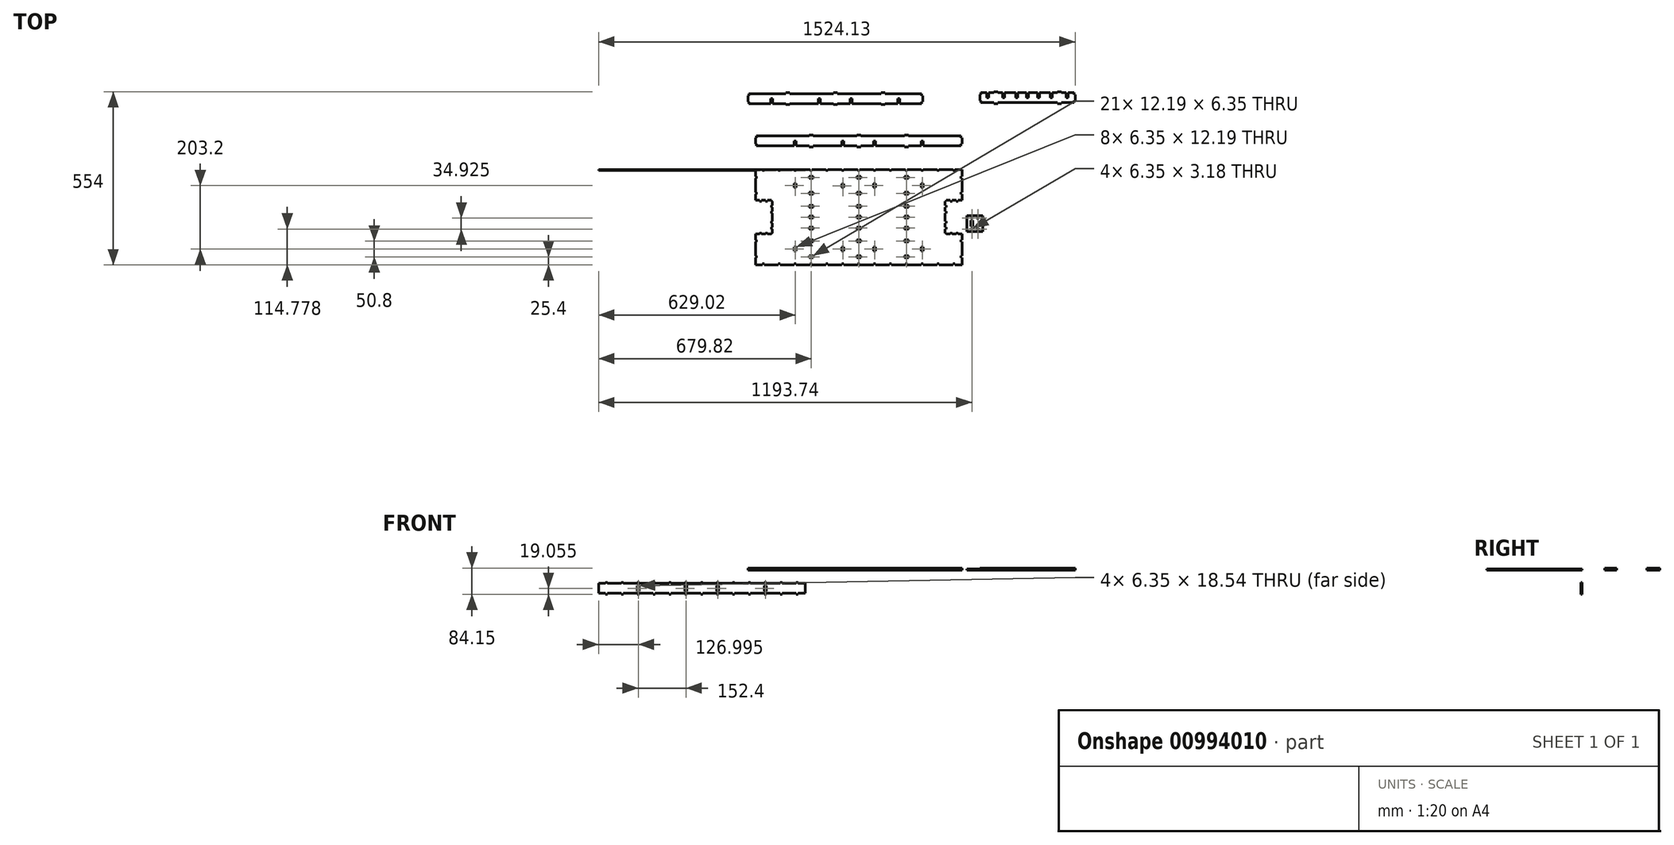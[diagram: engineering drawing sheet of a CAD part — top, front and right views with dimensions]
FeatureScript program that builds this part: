
annotation { "Feature Type Name" : "Feature", "Feature Type Description" : "" }
export const myFeature = defineFeature(function(context is Context, id is Id, definition is map)
    precondition{}
    {
        {
            var Q0;
            Q0=qCreatedBy(makeId("Top.planeOp"),FACE);
            var sketch = newSketch(context, id + "F0", { "sketchPlane" : qUnion([Q0])});
            skLineSegment(sketch, "E0", {"start": v(0, -98.43) * mm, "end": v(12.7, -98.43) * mm});
            skLineSegment(sketch, "E1", {"start": v(12.7, -98.43) * mm, "end": v(12.7, -101.6) * mm});
            skLineSegment(sketch, "E2", {"start": v(12.7, -101.6) * mm, "end": v(19.05, -101.6) * mm});
            skLineSegment(sketch, "E3", {"start": v(19.05, -101.6) * mm, "end": v(19.05, -98.43) * mm});
            skLineSegment(sketch, "E4", {"start": v(19.05, -98.43) * mm, "end": v(31.75, -98.43) * mm});
            skLineSegment(sketch, "E5", {"start": v(31.75, -98.43) * mm, "end": v(31.75, -101.6) * mm});
            skLineSegment(sketch, "E6", {"start": v(31.75, -101.6) * mm, "end": v(38.1, -101.6) * mm});
            skLineSegment(sketch, "E7", {"start": v(38.1, -101.6) * mm, "end": v(38.1, -98.43) * mm});
            skLineSegment(sketch, "E8", {"start": v(38.1, -98.43) * mm, "end": v(50.8, -98.43) * mm});
            skLineSegment(sketch, "E9", {"start": v(50.8, -98.43) * mm, "end": v(50.8, -101.6) * mm});
            skLineSegment(sketch, "E10", {"start": v(50.8, -101.6) * mm, "end": v(53.98, -101.6) * mm});
            skLineSegment(sketch, "E11", {"start": v(53.98, -101.6) * mm, "end": v(53.98, -114.3) * mm});
            skLineSegment(sketch, "E12", {"start": v(53.98, -114.3) * mm, "end": v(50.8, -114.3) * mm});
            skLineSegment(sketch, "E13", {"start": v(50.8, -114.3) * mm, "end": v(50.8, -120.65) * mm});
            skLineSegment(sketch, "E14", {"start": v(50.8, -120.65) * mm, "end": v(53.98, -120.65) * mm});
            skLineSegment(sketch, "E15", {"start": v(53.98, -120.65) * mm, "end": v(53.98, -133.35) * mm});
            skLineSegment(sketch, "E16", {"start": v(53.98, -133.35) * mm, "end": v(50.8, -133.35) * mm});
            skLineSegment(sketch, "E17", {"start": v(50.8, -133.35) * mm, "end": v(50.8, -139.7) * mm});
            skLineSegment(sketch, "E18", {"start": v(50.8, -139.7) * mm, "end": v(53.98, -139.7) * mm});
            skLineSegment(sketch, "E19", {"start": v(53.98, -139.7) * mm, "end": v(53.98, -152.4) * mm});
            skLineSegment(sketch, "E20", {"start": v(53.97, -152.4) * mm, "end": v(53.97, -165.1) * mm});
            skLineSegment(sketch, "E21", {"start": v(53.98, -165.1) * mm, "end": v(50.8, -165.1) * mm});
            skLineSegment(sketch, "E22", {"start": v(50.8, -165.1) * mm, "end": v(50.8, -171.45) * mm});
            skLineSegment(sketch, "E23", {"start": v(50.8, -171.45) * mm, "end": v(53.98, -171.45) * mm});
            skLineSegment(sketch, "E24", {"start": v(53.97, -171.45) * mm, "end": v(53.97, -184.15) * mm});
            skLineSegment(sketch, "E25", {"start": v(53.98, -184.15) * mm, "end": v(50.8, -184.15) * mm});
            skLineSegment(sketch, "E26", {"start": v(50.8, -184.15) * mm, "end": v(50.8, -190.5) * mm});
            skLineSegment(sketch, "E27", {"start": v(50.8, -190.5) * mm, "end": v(53.98, -190.5) * mm});
            skLineSegment(sketch, "E28", {"start": v(53.97, -190.5) * mm, "end": v(53.97, -203.2) * mm});
            skLineSegment(sketch, "E29", {"start": v(50.8, -206.38) * mm, "end": v(38.1, -206.38) * mm});
            skLineSegment(sketch, "E30", {"start": v(38.1, -206.38) * mm, "end": v(38.1, -203.2) * mm});
            skLineSegment(sketch, "E31", {"start": v(38.1, -203.2) * mm, "end": v(31.75, -203.2) * mm});
            skLineSegment(sketch, "E32", {"start": v(31.75, -203.2) * mm, "end": v(31.75, -206.38) * mm});
            skLineSegment(sketch, "E33", {"start": v(31.75, -206.38) * mm, "end": v(19.05, -206.38) * mm});
            skLineSegment(sketch, "E34", {"start": v(19.05, -206.38) * mm, "end": v(19.05, -203.2) * mm});
            skLineSegment(sketch, "E35", {"start": v(19.05, -203.2) * mm, "end": v(12.7, -203.2) * mm});
            skLineSegment(sketch, "E36", {"start": v(12.7, -203.2) * mm, "end": v(12.7, -206.38) * mm});
            skLineSegment(sketch, "E37", {"start": v(12.7, -206.38) * mm, "end": v(0, -206.38) * mm});
            skLineSegment(sketch, "E38", {"start": v(50.8, -206.38) * mm, "end": v(50.8, -203.2) * mm});
            skLineSegment(sketch, "E39", {"start": v(50.8, -203.2) * mm, "end": v(53.97, -203.2) * mm});
            skLineSegment(sketch, "E40", {"start": v(660.4, -206.38) * mm, "end": v(647.7, -206.38) * mm});
            skLineSegment(sketch, "E41", {"start": v(647.7, -206.38) * mm, "end": v(647.7, -203.2) * mm});
            skLineSegment(sketch, "E42", {"start": v(647.7, -203.2) * mm, "end": v(641.35, -203.2) * mm});
            skLineSegment(sketch, "E43", {"start": v(641.35, -203.2) * mm, "end": v(641.35, -206.38) * mm});
            skLineSegment(sketch, "E44", {"start": v(641.35, -206.38) * mm, "end": v(628.65, -206.38) * mm});
            skLineSegment(sketch, "E45", {"start": v(628.65, -206.38) * mm, "end": v(628.65, -203.2) * mm});
            skLineSegment(sketch, "E46", {"start": v(628.65, -203.2) * mm, "end": v(622.3, -203.2) * mm});
            skLineSegment(sketch, "E47", {"start": v(622.3, -203.2) * mm, "end": v(622.3, -206.38) * mm});
            skLineSegment(sketch, "E48", {"start": v(622.3, -206.38) * mm, "end": v(609.6, -206.38) * mm});
            skLineSegment(sketch, "E49", {"start": v(609.6, -206.38) * mm, "end": v(609.6, -203.2) * mm});
            skLineSegment(sketch, "E50", {"start": v(609.6, -203.2) * mm, "end": v(606.43, -203.2) * mm});
            skLineSegment(sketch, "E51", {"start": v(606.43, -203.2) * mm, "end": v(606.43, -190.5) * mm});
            skLineSegment(sketch, "E52", {"start": v(606.43, -190.5) * mm, "end": v(609.6, -190.5) * mm});
            skLineSegment(sketch, "E53", {"start": v(609.6, -190.5) * mm, "end": v(609.6, -184.15) * mm});
            skLineSegment(sketch, "E54", {"start": v(609.6, -184.15) * mm, "end": v(606.43, -184.15) * mm});
            skLineSegment(sketch, "E55", {"start": v(606.43, -184.15) * mm, "end": v(606.43, -171.45) * mm});
            skLineSegment(sketch, "E56", {"start": v(606.43, -171.45) * mm, "end": v(609.6, -171.45) * mm});
            skLineSegment(sketch, "E57", {"start": v(609.6, -171.45) * mm, "end": v(609.6, -165.1) * mm});
            skLineSegment(sketch, "E58", {"start": v(609.6, -165.1) * mm, "end": v(606.43, -165.1) * mm});
            skLineSegment(sketch, "E59", {"start": v(606.43, -165.1) * mm, "end": v(606.43, -152.4) * mm});
            skLineSegment(sketch, "E60", {"start": v(606.43, -152.4) * mm, "end": v(606.43, -139.7) * mm});
            skLineSegment(sketch, "E61", {"start": v(606.43, -139.7) * mm, "end": v(609.6, -139.7) * mm});
            skLineSegment(sketch, "E62", {"start": v(609.6, -139.7) * mm, "end": v(609.6, -133.35) * mm});
            skLineSegment(sketch, "E63", {"start": v(609.6, -133.35) * mm, "end": v(606.43, -133.35) * mm});
            skLineSegment(sketch, "E64", {"start": v(606.43, -133.35) * mm, "end": v(606.43, -120.65) * mm});
            skLineSegment(sketch, "E65", {"start": v(606.43, -120.65) * mm, "end": v(609.6, -120.65) * mm});
            skLineSegment(sketch, "E66", {"start": v(609.6, -120.65) * mm, "end": v(609.6, -114.3) * mm});
            skLineSegment(sketch, "E67", {"start": v(609.6, -114.3) * mm, "end": v(606.43, -114.3) * mm});
            skLineSegment(sketch, "E68", {"start": v(606.43, -114.3) * mm, "end": v(606.43, -101.6) * mm});
            skLineSegment(sketch, "E69", {"start": v(609.6, -98.43) * mm, "end": v(622.3, -98.43) * mm});
            skLineSegment(sketch, "E70", {"start": v(622.3, -98.42) * mm, "end": v(622.3, -101.6) * mm});
            skLineSegment(sketch, "E71", {"start": v(622.3, -101.6) * mm, "end": v(628.65, -101.6) * mm});
            skLineSegment(sketch, "E72", {"start": v(628.65, -101.6) * mm, "end": v(628.65, -98.42) * mm});
            skLineSegment(sketch, "E73", {"start": v(628.65, -98.42) * mm, "end": v(641.35, -98.42) * mm});
            skLineSegment(sketch, "E74", {"start": v(641.35, -98.42) * mm, "end": v(641.35, -101.6) * mm});
            skLineSegment(sketch, "E75", {"start": v(641.35, -101.6) * mm, "end": v(647.7, -101.6) * mm});
            skLineSegment(sketch, "E76", {"start": v(647.7, -101.6) * mm, "end": v(647.7, -98.42) * mm});
            skLineSegment(sketch, "E77", {"start": v(647.7, -98.42) * mm, "end": v(660.4, -98.42) * mm});
            skLineSegment(sketch, "E78", {"start": v(609.6, -98.43) * mm, "end": v(609.6, -101.6) * mm});
            skLineSegment(sketch, "E79", {"start": v(609.6, -101.6) * mm, "end": v(606.43, -101.6) * mm});
            skLineSegment(sketch, "E80", {"start": v(660.4, 0) * mm, "end": v(660.4, -22.22) * mm});
            skLineSegment(sketch, "E81", {"start": v(660.4, -22.22) * mm, "end": v(657.23, -22.22) * mm});
            skLineSegment(sketch, "E82", {"start": v(657.23, -22.22) * mm, "end": v(657.23, -28.57) * mm});
            skLineSegment(sketch, "E83", {"start": v(657.23, -28.57) * mm, "end": v(660.4, -28.57) * mm});
            skLineSegment(sketch, "E84", {"start": v(660.4, -28.57) * mm, "end": v(660.4, -50.8) * mm});
            skLineSegment(sketch, "E85", {"start": v(660.4, -50.8) * mm, "end": v(660.4, -73.02) * mm});
            skLineSegment(sketch, "E86", {"start": v(660.4, -73.02) * mm, "end": v(657.23, -73.02) * mm});
            skLineSegment(sketch, "E87", {"start": v(657.23, -73.02) * mm, "end": v(657.23, -79.37) * mm});
            skLineSegment(sketch, "E88", {"start": v(657.23, -79.37) * mm, "end": v(660.4, -79.37) * mm});
            skLineSegment(sketch, "E89", {"start": v(609.6, 0) * mm, "end": v(631.82, 0) * mm});
            skLineSegment(sketch, "E90", {"start": v(631.83, 0) * mm, "end": v(631.83, -3.17) * mm});
            skLineSegment(sketch, "E91", {"start": v(631.82, -3.17) * mm, "end": v(638.18, -3.17) * mm});
            skLineSegment(sketch, "E92", {"start": v(638.18, -3.17) * mm, "end": v(638.18, 0) * mm});
            skLineSegment(sketch, "E93", {"start": v(638.18, 0) * mm, "end": v(660.4, 0) * mm});
            skLineSegment(sketch, "E94", {"start": v(558.8, 0) * mm, "end": v(581.02, 0) * mm});
            skLineSegment(sketch, "E95", {"start": v(581.02, 0) * mm, "end": v(581.02, -3.17) * mm});
            skLineSegment(sketch, "E96", {"start": v(581.02, -3.17) * mm, "end": v(587.37, -3.17) * mm});
            skLineSegment(sketch, "E97", {"start": v(587.38, -3.17) * mm, "end": v(587.38, 0) * mm});
            skLineSegment(sketch, "E98", {"start": v(587.37, 0) * mm, "end": v(609.6, 0) * mm});
            skLineSegment(sketch, "E99", {"start": v(508, 0) * mm, "end": v(530.22, 0) * mm});
            skLineSegment(sketch, "E100", {"start": v(530.22, 0) * mm, "end": v(530.22, -3.18) * mm});
            skLineSegment(sketch, "E101", {"start": v(530.22, -3.18) * mm, "end": v(536.57, -3.18) * mm});
            skLineSegment(sketch, "E102", {"start": v(536.57, -3.18) * mm, "end": v(536.57, 0) * mm});
            skLineSegment(sketch, "E103", {"start": v(536.57, 0) * mm, "end": v(558.8, 0) * mm});
            skLineSegment(sketch, "E104", {"start": v(101.6, 0) * mm, "end": v(123.82, 0) * mm});
            skLineSegment(sketch, "E105", {"start": v(123.82, 0) * mm, "end": v(123.82, -3.17) * mm});
            skLineSegment(sketch, "E106", {"start": v(123.82, -3.17) * mm, "end": v(130.17, -3.17) * mm});
            skLineSegment(sketch, "E107", {"start": v(130.17, -3.17) * mm, "end": v(130.17, 0) * mm});
            skLineSegment(sketch, "E108", {"start": v(130.17, 0) * mm, "end": v(152.4, 0) * mm});
            skLineSegment(sketch, "E109", {"start": v(50.8, 0) * mm, "end": v(73.02, 0) * mm});
            skLineSegment(sketch, "E110", {"start": v(73.03, 0) * mm, "end": v(73.03, -3.17) * mm});
            skLineSegment(sketch, "E111", {"start": v(73.02, -3.17) * mm, "end": v(79.37, -3.17) * mm});
            skLineSegment(sketch, "E112", {"start": v(79.38, -3.17) * mm, "end": v(79.38, 0) * mm});
            skLineSegment(sketch, "E113", {"start": v(79.37, 0) * mm, "end": v(101.6, 0) * mm});
            skLineSegment(sketch, "E114", {"start": v(0, 0) * mm, "end": v(22.23, 0) * mm});
            skLineSegment(sketch, "E115", {"start": v(22.23, 0) * mm, "end": v(22.23, -3.18) * mm});
            skLineSegment(sketch, "E116", {"start": v(22.22, -3.18) * mm, "end": v(28.58, -3.18) * mm});
            skLineSegment(sketch, "E117", {"start": v(28.58, -3.18) * mm, "end": v(28.58, 0) * mm});
            skLineSegment(sketch, "E118", {"start": v(28.57, 0) * mm, "end": v(50.8, 0) * mm});
            skLineSegment(sketch, "E119", {"start": v(254, 0) * mm, "end": v(276.22, 0) * mm});
            skLineSegment(sketch, "E120", {"start": v(276.23, 0) * mm, "end": v(276.23, -3.17) * mm});
            skLineSegment(sketch, "E121", {"start": v(276.22, -3.17) * mm, "end": v(282.57, -3.17) * mm});
            skLineSegment(sketch, "E122", {"start": v(282.57, -3.17) * mm, "end": v(282.57, 0) * mm});
            skLineSegment(sketch, "E123", {"start": v(282.57, 0) * mm, "end": v(304.8, 0) * mm});
            skLineSegment(sketch, "E124", {"start": v(203.2, 0) * mm, "end": v(225.42, 0) * mm});
            skLineSegment(sketch, "E125", {"start": v(225.42, 0) * mm, "end": v(225.42, -3.17) * mm});
            skLineSegment(sketch, "E126", {"start": v(225.42, -3.17) * mm, "end": v(231.77, -3.17) * mm});
            skLineSegment(sketch, "E127", {"start": v(231.77, -3.17) * mm, "end": v(231.77, 0) * mm});
            skLineSegment(sketch, "E128", {"start": v(231.77, 0) * mm, "end": v(254, 0) * mm});
            skLineSegment(sketch, "E129", {"start": v(152.4, 0) * mm, "end": v(174.62, 0) * mm});
            skLineSegment(sketch, "E130", {"start": v(174.62, 0) * mm, "end": v(174.62, -3.17) * mm});
            skLineSegment(sketch, "E131", {"start": v(174.62, -3.17) * mm, "end": v(180.97, -3.17) * mm});
            skLineSegment(sketch, "E132", {"start": v(180.97, -3.17) * mm, "end": v(180.97, 0) * mm});
            skLineSegment(sketch, "E133", {"start": v(180.97, 0) * mm, "end": v(203.2, 0) * mm});
            skLineSegment(sketch, "E134", {"start": v(406.4, 0) * mm, "end": v(428.62, 0) * mm});
            skLineSegment(sketch, "E135", {"start": v(428.63, 0) * mm, "end": v(428.63, -3.17) * mm});
            skLineSegment(sketch, "E136", {"start": v(428.62, -3.17) * mm, "end": v(434.97, -3.17) * mm});
            skLineSegment(sketch, "E137", {"start": v(434.98, -3.17) * mm, "end": v(434.98, 0) * mm});
            skLineSegment(sketch, "E138", {"start": v(434.98, 0) * mm, "end": v(457.2, 0) * mm});
            skLineSegment(sketch, "E139", {"start": v(355.6, 0) * mm, "end": v(377.82, 0) * mm});
            skLineSegment(sketch, "E140", {"start": v(377.83, 0) * mm, "end": v(377.83, -3.17) * mm});
            skLineSegment(sketch, "E141", {"start": v(377.82, -3.17) * mm, "end": v(384.17, -3.17) * mm});
            skLineSegment(sketch, "E142", {"start": v(384.18, -3.17) * mm, "end": v(384.18, 0) * mm});
            skLineSegment(sketch, "E143", {"start": v(384.17, 0) * mm, "end": v(406.4, 0) * mm});
            skLineSegment(sketch, "E144", {"start": v(304.8, 0) * mm, "end": v(327.02, 0) * mm});
            skLineSegment(sketch, "E145", {"start": v(327.03, 0) * mm, "end": v(327.03, -3.17) * mm});
            skLineSegment(sketch, "E146", {"start": v(327.02, -3.17) * mm, "end": v(333.37, -3.17) * mm});
            skLineSegment(sketch, "E147", {"start": v(333.38, -3.17) * mm, "end": v(333.38, 0) * mm});
            skLineSegment(sketch, "E148", {"start": v(333.37, 0) * mm, "end": v(355.6, 0) * mm});
            skLineSegment(sketch, "E149", {"start": v(457.2, 0) * mm, "end": v(479.42, 0) * mm});
            skLineSegment(sketch, "E150", {"start": v(479.43, 0) * mm, "end": v(479.43, -3.17) * mm});
            skLineSegment(sketch, "E151", {"start": v(479.42, -3.17) * mm, "end": v(485.77, -3.17) * mm});
            skLineSegment(sketch, "E152", {"start": v(485.78, -3.17) * mm, "end": v(485.78, 0) * mm});
            skLineSegment(sketch, "E153", {"start": v(50.8, -304.8) * mm, "end": v(28.58, -304.8) * mm});
            skLineSegment(sketch, "E154", {"start": v(28.57, -304.8) * mm, "end": v(28.57, -301.62) * mm});
            skLineSegment(sketch, "E155", {"start": v(28.58, -301.62) * mm, "end": v(22.23, -301.62) * mm});
            skLineSegment(sketch, "E156", {"start": v(22.22, -301.62) * mm, "end": v(22.22, -304.8) * mm});
            skLineSegment(sketch, "E157", {"start": v(22.22, -304.8) * mm, "end": v(0, -304.8) * mm});
            skLineSegment(sketch, "E158", {"start": v(101.6, -304.8) * mm, "end": v(79.38, -304.8) * mm});
            skLineSegment(sketch, "E159", {"start": v(79.38, -304.8) * mm, "end": v(79.38, -301.62) * mm});
            skLineSegment(sketch, "E160", {"start": v(79.38, -301.62) * mm, "end": v(73.03, -301.62) * mm});
            skLineSegment(sketch, "E161", {"start": v(73.03, -301.62) * mm, "end": v(73.03, -304.8) * mm});
            skLineSegment(sketch, "E162", {"start": v(73.03, -304.8) * mm, "end": v(50.8, -304.8) * mm});
            skLineSegment(sketch, "E163", {"start": v(152.4, -304.8) * mm, "end": v(130.18, -304.8) * mm});
            skLineSegment(sketch, "E164", {"start": v(130.18, -304.8) * mm, "end": v(130.18, -301.62) * mm});
            skLineSegment(sketch, "E165", {"start": v(130.18, -301.62) * mm, "end": v(123.83, -301.62) * mm});
            skLineSegment(sketch, "E166", {"start": v(123.83, -301.62) * mm, "end": v(123.83, -304.8) * mm});
            skLineSegment(sketch, "E167", {"start": v(123.83, -304.8) * mm, "end": v(101.6, -304.8) * mm});
            skLineSegment(sketch, "E168", {"start": v(558.8, -304.8) * mm, "end": v(536.58, -304.8) * mm});
            skLineSegment(sketch, "E169", {"start": v(536.57, -304.8) * mm, "end": v(536.57, -301.62) * mm});
            skLineSegment(sketch, "E170", {"start": v(536.58, -301.62) * mm, "end": v(530.22, -301.62) * mm});
            skLineSegment(sketch, "E171", {"start": v(530.22, -301.62) * mm, "end": v(530.22, -304.8) * mm});
            skLineSegment(sketch, "E172", {"start": v(530.22, -304.8) * mm, "end": v(508, -304.8) * mm});
            skLineSegment(sketch, "E173", {"start": v(609.6, -304.8) * mm, "end": v(587.37, -304.8) * mm});
            skLineSegment(sketch, "E174", {"start": v(587.38, -304.8) * mm, "end": v(587.38, -301.62) * mm});
            skLineSegment(sketch, "E175", {"start": v(587.38, -301.62) * mm, "end": v(581.02, -301.62) * mm});
            skLineSegment(sketch, "E176", {"start": v(581.02, -301.62) * mm, "end": v(581.02, -304.8) * mm});
            skLineSegment(sketch, "E177", {"start": v(581.02, -304.8) * mm, "end": v(558.8, -304.8) * mm});
            skLineSegment(sketch, "E178", {"start": v(660.4, -304.8) * mm, "end": v(638.18, -304.8) * mm});
            skLineSegment(sketch, "E179", {"start": v(638.17, -304.8) * mm, "end": v(638.17, -301.62) * mm});
            skLineSegment(sketch, "E180", {"start": v(638.18, -301.62) * mm, "end": v(631.82, -301.62) * mm});
            skLineSegment(sketch, "E181", {"start": v(631.83, -301.62) * mm, "end": v(631.83, -304.8) * mm});
            skLineSegment(sketch, "E182", {"start": v(631.83, -304.8) * mm, "end": v(609.6, -304.8) * mm});
            skLineSegment(sketch, "E183", {"start": v(406.4, -304.8) * mm, "end": v(384.17, -304.8) * mm});
            skLineSegment(sketch, "E184", {"start": v(384.17, -304.8) * mm, "end": v(384.17, -301.62) * mm});
            skLineSegment(sketch, "E185", {"start": v(384.17, -301.62) * mm, "end": v(377.82, -301.62) * mm});
            skLineSegment(sketch, "E186", {"start": v(377.82, -301.62) * mm, "end": v(377.82, -304.8) * mm});
            skLineSegment(sketch, "E187", {"start": v(377.82, -304.8) * mm, "end": v(355.6, -304.8) * mm});
            skLineSegment(sketch, "E188", {"start": v(457.2, -304.8) * mm, "end": v(434.97, -304.8) * mm});
            skLineSegment(sketch, "E189", {"start": v(434.97, -304.8) * mm, "end": v(434.97, -301.62) * mm});
            skLineSegment(sketch, "E190", {"start": v(434.97, -301.62) * mm, "end": v(428.62, -301.62) * mm});
            skLineSegment(sketch, "E191", {"start": v(428.62, -301.62) * mm, "end": v(428.62, -304.8) * mm});
            skLineSegment(sketch, "E192", {"start": v(428.62, -304.8) * mm, "end": v(406.4, -304.8) * mm});
            skLineSegment(sketch, "E193", {"start": v(508, -304.8) * mm, "end": v(485.77, -304.8) * mm});
            skLineSegment(sketch, "E194", {"start": v(485.77, -304.8) * mm, "end": v(485.77, -301.62) * mm});
            skLineSegment(sketch, "E195", {"start": v(485.77, -301.62) * mm, "end": v(479.42, -301.62) * mm});
            skLineSegment(sketch, "E196", {"start": v(479.42, -301.62) * mm, "end": v(479.42, -304.8) * mm});
            skLineSegment(sketch, "E197", {"start": v(479.42, -304.8) * mm, "end": v(457.2, -304.8) * mm});
            skLineSegment(sketch, "E198", {"start": v(254, -304.8) * mm, "end": v(231.77, -304.8) * mm});
            skLineSegment(sketch, "E199", {"start": v(231.77, -304.8) * mm, "end": v(231.77, -301.62) * mm});
            skLineSegment(sketch, "E200", {"start": v(231.77, -301.62) * mm, "end": v(225.42, -301.62) * mm});
            skLineSegment(sketch, "E201", {"start": v(225.42, -301.62) * mm, "end": v(225.42, -304.8) * mm});
            skLineSegment(sketch, "E202", {"start": v(225.42, -304.8) * mm, "end": v(203.2, -304.8) * mm});
            skLineSegment(sketch, "E203", {"start": v(304.8, -304.8) * mm, "end": v(282.57, -304.8) * mm});
            skLineSegment(sketch, "E204", {"start": v(282.57, -304.8) * mm, "end": v(282.57, -301.62) * mm});
            skLineSegment(sketch, "E205", {"start": v(282.57, -301.62) * mm, "end": v(276.22, -301.62) * mm});
            skLineSegment(sketch, "E206", {"start": v(276.22, -301.62) * mm, "end": v(276.22, -304.8) * mm});
            skLineSegment(sketch, "E207", {"start": v(276.22, -304.8) * mm, "end": v(254, -304.8) * mm});
            skLineSegment(sketch, "E208", {"start": v(355.6, -304.8) * mm, "end": v(333.37, -304.8) * mm});
            skLineSegment(sketch, "E209", {"start": v(333.37, -304.8) * mm, "end": v(333.37, -301.62) * mm});
            skLineSegment(sketch, "E210", {"start": v(333.37, -301.62) * mm, "end": v(327.02, -301.62) * mm});
            skLineSegment(sketch, "E211", {"start": v(327.02, -301.62) * mm, "end": v(327.02, -304.8) * mm});
            skLineSegment(sketch, "E212", {"start": v(327.02, -304.8) * mm, "end": v(304.8, -304.8) * mm});
            skLineSegment(sketch, "E213", {"start": v(203.2, -304.8) * mm, "end": v(180.97, -304.8) * mm});
            skLineSegment(sketch, "E214", {"start": v(180.97, -304.8) * mm, "end": v(180.97, -301.62) * mm});
            skLineSegment(sketch, "E215", {"start": v(180.97, -301.62) * mm, "end": v(174.62, -301.62) * mm});
            skLineSegment(sketch, "E216", {"start": v(174.62, -301.62) * mm, "end": v(174.62, -304.8) * mm});
            skLineSegment(sketch, "E217", {"start": v(174.62, -304.8) * mm, "end": v(152.4, -304.8) * mm});
            skLineSegment(sketch, "E218", {"start": v(660.4, -225.42) * mm, "end": v(657.23, -225.42) * mm});
            skLineSegment(sketch, "E219", {"start": v(657.23, -225.42) * mm, "end": v(657.23, -231.77) * mm});
            skLineSegment(sketch, "E220", {"start": v(657.23, -231.77) * mm, "end": v(660.4, -231.77) * mm});
            skLineSegment(sketch, "E221", {"start": v(660.4, -231.77) * mm, "end": v(660.4, -254) * mm});
            skLineSegment(sketch, "E222", {"start": v(660.4, -254) * mm, "end": v(660.4, -276.22) * mm});
            skLineSegment(sketch, "E223", {"start": v(660.4, -276.22) * mm, "end": v(657.23, -276.22) * mm});
            skLineSegment(sketch, "E224", {"start": v(657.23, -276.22) * mm, "end": v(657.23, -282.57) * mm});
            skLineSegment(sketch, "E225", {"start": v(657.23, -282.57) * mm, "end": v(660.4, -282.57) * mm});
            skLineSegment(sketch, "E226", {"start": v(660.4, -282.57) * mm, "end": v(660.4, -304.8) * mm});
            skLineSegment(sketch, "E227", {"start": v(0, -79.38) * mm, "end": v(3.18, -79.38) * mm});
            skLineSegment(sketch, "E228", {"start": v(3.18, -79.38) * mm, "end": v(3.18, -73.03) * mm});
            skLineSegment(sketch, "E229", {"start": v(3.18, -73.03) * mm, "end": v(0, -73.03) * mm});
            skLineSegment(sketch, "E230", {"start": v(0, -73.03) * mm, "end": v(0, -50.8) * mm});
            skLineSegment(sketch, "E231", {"start": v(0, -50.8) * mm, "end": v(0, -28.58) * mm});
            skLineSegment(sketch, "E232", {"start": v(0, -28.58) * mm, "end": v(3.18, -28.58) * mm});
            skLineSegment(sketch, "E233", {"start": v(3.18, -28.58) * mm, "end": v(3.18, -22.22) * mm});
            skLineSegment(sketch, "E234", {"start": v(3.18, -22.22) * mm, "end": v(0, -22.22) * mm});
            skLineSegment(sketch, "E235", {"start": v(0, -22.22) * mm, "end": v(0, 0) * mm});
            skLineSegment(sketch, "E236", {"start": v(0, -304.8) * mm, "end": v(0, -282.58) * mm});
            skLineSegment(sketch, "E237", {"start": v(0, -282.58) * mm, "end": v(3.18, -282.58) * mm});
            skLineSegment(sketch, "E238", {"start": v(3.18, -282.57) * mm, "end": v(3.18, -276.23) * mm});
            skLineSegment(sketch, "E239", {"start": v(3.18, -276.23) * mm, "end": v(0, -276.23) * mm});
            skLineSegment(sketch, "E240", {"start": v(0, -276.23) * mm, "end": v(0, -254) * mm});
            skLineSegment(sketch, "E241", {"start": v(0, -254) * mm, "end": v(0, -231.78) * mm});
            skLineSegment(sketch, "E242", {"start": v(0, -231.78) * mm, "end": v(3.18, -231.78) * mm});
            skLineSegment(sketch, "E243", {"start": v(3.18, -231.78) * mm, "end": v(3.18, -225.43) * mm});
            skLineSegment(sketch, "E244", {"start": v(3.18, -225.42) * mm, "end": v(0, -225.42) * mm});
            skPoint(sketch, "E245.startSnap0", {"position": v(50.8, -117.48) * mm});
            skPoint(sketch, "E246", {"position": v(50.8, -187.33) * mm});
            skPoint(sketch, "E247.middle.positionSnap0", {"position": v(25.4, -3.18) * mm});
            skPoint(sketch, "E247.centerSnap0", {"position": v(25.4, -3.18) * mm});
            skPoint(sketch, "E248.middle.positionSnap0", {"position": v(76.2, -3.17) * mm});
            skPoint(sketch, "E248.centerSnap0", {"position": v(76.2, -3.17) * mm});
            skPoint(sketch, "E249.middle.positionSnap0", {"position": v(177.8, -3.17) * mm});
            skPoint(sketch, "E249.centerSnap0", {"position": v(177.8, -3.17) * mm});
            skPoint(sketch, "E250.middle.positionSnap0", {"position": v(279.4, -3.17) * mm});
            skPoint(sketch, "E250.centerSnap0", {"position": v(279.4, -3.17) * mm});
            skPoint(sketch, "E251.middle.positionSnap0", {"position": v(381, -3.17) * mm});
            skPoint(sketch, "E251.centerSnap0", {"position": v(381, -3.17) * mm});
            skPoint(sketch, "E252.middle.positionSnap0", {"position": v(482.6, -3.17) * mm});
            skPoint(sketch, "E252.centerSnap0", {"position": v(482.6, -3.17) * mm});
            skPoint(sketch, "E253.middle.positionSnap0", {"position": v(584.2, -3.17) * mm});
            skPoint(sketch, "E253.centerSnap0", {"position": v(584.2, -3.17) * mm});
            skPoint(sketch, "E254.middle.positionSnap0", {"position": v(635, -3.17) * mm});
            skPoint(sketch, "E254.centerSnap0", {"position": v(635, -3.17) * mm});
            skPoint(sketch, "E255", {"position": v(25.4, -206.38) * mm});
            skPoint(sketch, "E256", {"position": v(533.4, -301.62) * mm});
            skLineSegment(sketch, "E257", {"start": v(0, -98.43) * mm, "end": v(0, -79.38) * mm});
            skLineSegment(sketch, "E258", {"start": v(660.4, -79.37) * mm, "end": v(660.4, -98.42) * mm});
            skLineSegment(sketch, "E259", {"start": v(660.4, -206.38) * mm, "end": v(660.4, -225.42) * mm});
            skLineSegment(sketch, "E260", {"start": v(0, -225.42) * mm, "end": v(0, -206.38) * mm});
            skLineSegment(sketch, "E261", {"start": v(485.78, 0) * mm, "end": v(508, 0) * mm});
            skPoint(sketch, "E262", {"position": v(3.18, -76.2) * mm});
            skLineSegment(sketch, "E263.bottom", {"start": v(183.9, -282.57) * mm, "end": v(171.7, -282.57) * mm});
            skLineSegment(sketch, "E263.top", {"start": v(183.9, -276.22) * mm, "end": v(171.7, -276.22) * mm});
            skLineSegment(sketch, "E263.left", {"start": v(183.9, -282.57) * mm, "end": v(183.9, -276.22) * mm});
            skLineSegment(sketch, "E263.right", {"start": v(171.7, -282.57) * mm, "end": v(171.7, -276.22) * mm});
            skPoint(sketch, "E263.middle", {"position": v(177.8, -279.4) * mm});
            skLineSegment(sketch, "E264.bottom", {"start": v(336.3, -282.57) * mm, "end": v(324.1, -282.57) * mm});
            skLineSegment(sketch, "E264.top", {"start": v(336.3, -276.22) * mm, "end": v(324.1, -276.22) * mm});
            skLineSegment(sketch, "E264.left", {"start": v(336.3, -282.57) * mm, "end": v(336.3, -276.22) * mm});
            skLineSegment(sketch, "E264.right", {"start": v(324.1, -282.57) * mm, "end": v(324.1, -276.22) * mm});
            skPoint(sketch, "E264.middle", {"position": v(330.2, -279.4) * mm});
            skLineSegment(sketch, "E265.bottom", {"start": v(488.7, -282.57) * mm, "end": v(476.5, -282.57) * mm});
            skLineSegment(sketch, "E265.top", {"start": v(488.7, -276.22) * mm, "end": v(476.5, -276.22) * mm});
            skLineSegment(sketch, "E265.left", {"start": v(488.7, -282.57) * mm, "end": v(488.7, -276.22) * mm});
            skLineSegment(sketch, "E265.right", {"start": v(476.5, -282.57) * mm, "end": v(476.5, -276.22) * mm});
            skPoint(sketch, "E265.middle", {"position": v(482.6, -279.4) * mm});
            skLineSegment(sketch, "E266.bottom", {"start": v(336.3, -231.78) * mm, "end": v(324.1, -231.78) * mm});
            skLineSegment(sketch, "E266.top", {"start": v(336.3, -225.42) * mm, "end": v(324.1, -225.42) * mm});
            skLineSegment(sketch, "E266.left", {"start": v(336.3, -231.78) * mm, "end": v(336.3, -225.42) * mm});
            skLineSegment(sketch, "E266.right", {"start": v(324.1, -231.78) * mm, "end": v(324.1, -225.42) * mm});
            skPoint(sketch, "E266.middle", {"position": v(330.2, -228.6) * mm});
            skLineSegment(sketch, "E267.bottom", {"start": v(183.9, -231.78) * mm, "end": v(171.7, -231.78) * mm});
            skLineSegment(sketch, "E267.top", {"start": v(183.9, -225.43) * mm, "end": v(171.7, -225.43) * mm});
            skLineSegment(sketch, "E267.left", {"start": v(183.9, -231.78) * mm, "end": v(183.9, -225.43) * mm});
            skLineSegment(sketch, "E267.right", {"start": v(171.7, -231.78) * mm, "end": v(171.7, -225.43) * mm});
            skPoint(sketch, "E267.middle", {"position": v(177.8, -228.6) * mm});
            skLineSegment(sketch, "E268.bottom", {"start": v(488.7, -231.77) * mm, "end": v(476.5, -231.77) * mm});
            skLineSegment(sketch, "E268.top", {"start": v(488.7, -225.42) * mm, "end": v(476.5, -225.42) * mm});
            skLineSegment(sketch, "E268.left", {"start": v(488.7, -231.77) * mm, "end": v(488.7, -225.42) * mm});
            skLineSegment(sketch, "E268.right", {"start": v(476.5, -231.77) * mm, "end": v(476.5, -225.42) * mm});
            skPoint(sketch, "E268.middle", {"position": v(482.6, -228.6) * mm});
            skLineSegment(sketch, "E269.bottom", {"start": v(336.3, -155.57) * mm, "end": v(324.1, -155.57) * mm});
            skLineSegment(sketch, "E269.top", {"start": v(336.3, -149.22) * mm, "end": v(324.1, -149.22) * mm});
            skLineSegment(sketch, "E269.left", {"start": v(336.3, -155.57) * mm, "end": v(336.3, -149.22) * mm});
            skLineSegment(sketch, "E269.right", {"start": v(324.1, -155.57) * mm, "end": v(324.1, -149.22) * mm});
            skPoint(sketch, "E269.middle", {"position": v(330.2, -152.4) * mm});
            skLineSegment(sketch, "E270.bottom", {"start": v(183.9, -155.57) * mm, "end": v(171.7, -155.57) * mm});
            skLineSegment(sketch, "E270.top", {"start": v(183.9, -149.22) * mm, "end": v(171.7, -149.22) * mm});
            skLineSegment(sketch, "E270.left", {"start": v(183.9, -155.57) * mm, "end": v(183.9, -149.22) * mm});
            skLineSegment(sketch, "E270.right", {"start": v(171.7, -155.57) * mm, "end": v(171.7, -149.22) * mm});
            skPoint(sketch, "E270.middle", {"position": v(177.8, -152.4) * mm});
            skLineSegment(sketch, "E271.bottom", {"start": v(488.7, -155.57) * mm, "end": v(476.5, -155.57) * mm});
            skLineSegment(sketch, "E271.top", {"start": v(488.7, -149.22) * mm, "end": v(476.5, -149.22) * mm});
            skLineSegment(sketch, "E271.left", {"start": v(488.7, -155.57) * mm, "end": v(488.7, -149.22) * mm});
            skLineSegment(sketch, "E271.right", {"start": v(476.5, -155.57) * mm, "end": v(476.5, -149.22) * mm});
            skPoint(sketch, "E271.middle", {"position": v(482.6, -152.4) * mm});
            skLineSegment(sketch, "E272.bottom", {"start": v(336.3, -79.37) * mm, "end": v(324.1, -79.37) * mm});
            skLineSegment(sketch, "E272.top", {"start": v(336.3, -73.02) * mm, "end": v(324.1, -73.02) * mm});
            skLineSegment(sketch, "E272.left", {"start": v(336.3, -79.37) * mm, "end": v(336.3, -73.02) * mm});
            skLineSegment(sketch, "E272.right", {"start": v(324.1, -79.37) * mm, "end": v(324.1, -73.02) * mm});
            skPoint(sketch, "E272.middle", {"position": v(330.2, -76.2) * mm});
            skLineSegment(sketch, "E273.bottom", {"start": v(183.9, -79.38) * mm, "end": v(171.7, -79.38) * mm});
            skLineSegment(sketch, "E273.top", {"start": v(183.9, -73.03) * mm, "end": v(171.7, -73.03) * mm});
            skLineSegment(sketch, "E273.left", {"start": v(183.9, -79.38) * mm, "end": v(183.9, -73.03) * mm});
            skLineSegment(sketch, "E273.right", {"start": v(171.7, -79.38) * mm, "end": v(171.7, -73.03) * mm});
            skPoint(sketch, "E273.middle", {"position": v(177.8, -76.2) * mm});
            skLineSegment(sketch, "E274.bottom", {"start": v(488.7, -79.37) * mm, "end": v(476.5, -79.37) * mm});
            skLineSegment(sketch, "E274.top", {"start": v(488.7, -73.02) * mm, "end": v(476.5, -73.02) * mm});
            skLineSegment(sketch, "E274.left", {"start": v(488.7, -79.37) * mm, "end": v(488.7, -73.02) * mm});
            skLineSegment(sketch, "E274.right", {"start": v(476.5, -79.37) * mm, "end": v(476.5, -73.02) * mm});
            skPoint(sketch, "E274.middle", {"position": v(482.6, -76.2) * mm});
            skLineSegment(sketch, "E275.bottom", {"start": v(336.3, -28.57) * mm, "end": v(324.1, -28.57) * mm});
            skLineSegment(sketch, "E275.top", {"start": v(336.3, -22.22) * mm, "end": v(324.1, -22.22) * mm});
            skLineSegment(sketch, "E275.left", {"start": v(336.3, -28.57) * mm, "end": v(336.3, -22.22) * mm});
            skLineSegment(sketch, "E275.right", {"start": v(324.1, -28.57) * mm, "end": v(324.1, -22.22) * mm});
            skPoint(sketch, "E275.middle", {"position": v(330.2, -25.4) * mm});
            skLineSegment(sketch, "E276.bottom", {"start": v(183.9, -28.58) * mm, "end": v(171.7, -28.58) * mm});
            skLineSegment(sketch, "E276.top", {"start": v(183.9, -22.23) * mm, "end": v(171.7, -22.23) * mm});
            skLineSegment(sketch, "E276.left", {"start": v(183.9, -28.58) * mm, "end": v(183.9, -22.23) * mm});
            skLineSegment(sketch, "E276.right", {"start": v(171.7, -28.58) * mm, "end": v(171.7, -22.23) * mm});
            skPoint(sketch, "E276.middle", {"position": v(177.8, -25.4) * mm});
            skLineSegment(sketch, "E277.bottom", {"start": v(488.7, -28.57) * mm, "end": v(476.5, -28.57) * mm});
            skLineSegment(sketch, "E277.top", {"start": v(488.7, -22.22) * mm, "end": v(476.5, -22.22) * mm});
            skLineSegment(sketch, "E277.left", {"start": v(488.7, -28.57) * mm, "end": v(488.7, -22.22) * mm});
            skLineSegment(sketch, "E277.right", {"start": v(476.5, -28.57) * mm, "end": v(476.5, -22.22) * mm});
            skPoint(sketch, "E277.middle", {"position": v(482.6, -25.4) * mm});
            skLineSegment(sketch, "E278.bottom", {"start": v(130.17, -56.9) * mm, "end": v(123.82, -56.9) * mm});
            skLineSegment(sketch, "E278.top", {"start": v(130.17, -44.7) * mm, "end": v(123.82, -44.7) * mm});
            skLineSegment(sketch, "E278.left", {"start": v(130.17, -56.9) * mm, "end": v(130.17, -44.7) * mm});
            skLineSegment(sketch, "E278.right", {"start": v(123.82, -56.9) * mm, "end": v(123.82, -44.7) * mm});
            skPoint(sketch, "E278.middle", {"position": v(127, -50.8) * mm});
            skLineSegment(sketch, "E279.bottom", {"start": v(282.58, -57.86) * mm, "end": v(276.23, -57.86) * mm});
            skLineSegment(sketch, "E279.top", {"start": v(282.58, -45.67) * mm, "end": v(276.23, -45.67) * mm});
            skLineSegment(sketch, "E279.left", {"start": v(282.58, -57.86) * mm, "end": v(282.58, -45.67) * mm});
            skLineSegment(sketch, "E279.right", {"start": v(276.23, -57.86) * mm, "end": v(276.23, -45.67) * mm});
            skPoint(sketch, "E279.middle", {"position": v(279.4, -51.77) * mm});
            skLineSegment(sketch, "E280.bottom", {"start": v(384.17, -56.9) * mm, "end": v(377.82, -56.9) * mm});
            skLineSegment(sketch, "E280.top", {"start": v(384.17, -44.7) * mm, "end": v(377.82, -44.7) * mm});
            skLineSegment(sketch, "E280.left", {"start": v(384.17, -56.9) * mm, "end": v(384.17, -44.7) * mm});
            skLineSegment(sketch, "E280.right", {"start": v(377.82, -56.9) * mm, "end": v(377.82, -44.7) * mm});
            skPoint(sketch, "E280.middle", {"position": v(381, -50.8) * mm});
            skLineSegment(sketch, "E281.bottom", {"start": v(536.57, -56.9) * mm, "end": v(530.22, -56.9) * mm});
            skLineSegment(sketch, "E281.top", {"start": v(536.57, -44.7) * mm, "end": v(530.22, -44.7) * mm});
            skLineSegment(sketch, "E281.left", {"start": v(536.57, -56.9) * mm, "end": v(536.57, -44.7) * mm});
            skLineSegment(sketch, "E281.right", {"start": v(530.22, -56.9) * mm, "end": v(530.22, -44.7) * mm});
            skPoint(sketch, "E281.middle", {"position": v(533.4, -50.8) * mm});
            skLineSegment(sketch, "E282.bottom", {"start": v(130.17, -260.1) * mm, "end": v(123.82, -260.1) * mm});
            skLineSegment(sketch, "E282.top", {"start": v(130.17, -247.9) * mm, "end": v(123.82, -247.9) * mm});
            skLineSegment(sketch, "E282.left", {"start": v(130.17, -260.1) * mm, "end": v(130.17, -247.9) * mm});
            skLineSegment(sketch, "E282.right", {"start": v(123.82, -260.1) * mm, "end": v(123.82, -247.9) * mm});
            skPoint(sketch, "E282.middle", {"position": v(127, -254) * mm});
            skLineSegment(sketch, "E283.bottom", {"start": v(282.57, -260.1) * mm, "end": v(276.22, -260.1) * mm});
            skLineSegment(sketch, "E283.top", {"start": v(282.57, -247.9) * mm, "end": v(276.22, -247.9) * mm});
            skLineSegment(sketch, "E283.left", {"start": v(282.57, -260.1) * mm, "end": v(282.57, -247.9) * mm});
            skLineSegment(sketch, "E283.right", {"start": v(276.22, -260.1) * mm, "end": v(276.22, -247.9) * mm});
            skPoint(sketch, "E283.middle", {"position": v(279.4, -254) * mm});
            skLineSegment(sketch, "E284.bottom", {"start": v(384.17, -260.1) * mm, "end": v(377.82, -260.1) * mm});
            skLineSegment(sketch, "E284.top", {"start": v(384.17, -247.9) * mm, "end": v(377.82, -247.9) * mm});
            skLineSegment(sketch, "E284.left", {"start": v(384.17, -260.1) * mm, "end": v(384.17, -247.9) * mm});
            skLineSegment(sketch, "E284.right", {"start": v(377.82, -260.1) * mm, "end": v(377.82, -247.9) * mm});
            skPoint(sketch, "E284.middle", {"position": v(381, -254) * mm});
            skLineSegment(sketch, "E285.bottom", {"start": v(536.57, -260.1) * mm, "end": v(530.22, -260.1) * mm});
            skLineSegment(sketch, "E285.top", {"start": v(536.57, -247.9) * mm, "end": v(530.22, -247.9) * mm});
            skLineSegment(sketch, "E285.left", {"start": v(536.57, -260.1) * mm, "end": v(536.57, -247.9) * mm});
            skLineSegment(sketch, "E285.right", {"start": v(530.22, -260.1) * mm, "end": v(530.22, -247.9) * mm});
            skPoint(sketch, "E285.middle", {"position": v(533.4, -254) * mm});
            skLineSegment(sketch, "E286.bottom", {"start": v(336.3, -120.65) * mm, "end": v(324.1, -120.65) * mm});
            skLineSegment(sketch, "E286.top", {"start": v(336.3, -114.3) * mm, "end": v(324.1, -114.3) * mm});
            skLineSegment(sketch, "E286.left", {"start": v(336.3, -120.65) * mm, "end": v(336.3, -114.3) * mm});
            skLineSegment(sketch, "E286.right", {"start": v(324.1, -120.65) * mm, "end": v(324.1, -114.3) * mm});
            skPoint(sketch, "E286.middle", {"position": v(330.2, -117.48) * mm});
            skLineSegment(sketch, "E287.bottom", {"start": v(183.9, -120.65) * mm, "end": v(171.7, -120.65) * mm});
            skLineSegment(sketch, "E287.top", {"start": v(183.9, -114.3) * mm, "end": v(171.7, -114.3) * mm});
            skLineSegment(sketch, "E287.left", {"start": v(183.9, -120.65) * mm, "end": v(183.9, -114.3) * mm});
            skLineSegment(sketch, "E287.right", {"start": v(171.7, -120.65) * mm, "end": v(171.7, -114.3) * mm});
            skPoint(sketch, "E287.middle", {"position": v(177.8, -117.48) * mm});
            skLineSegment(sketch, "E288.bottom", {"start": v(488.7, -120.65) * mm, "end": v(476.5, -120.65) * mm});
            skLineSegment(sketch, "E288.top", {"start": v(488.7, -114.3) * mm, "end": v(476.5, -114.3) * mm});
            skLineSegment(sketch, "E288.left", {"start": v(488.7, -120.65) * mm, "end": v(488.7, -114.3) * mm});
            skLineSegment(sketch, "E288.right", {"start": v(476.5, -120.65) * mm, "end": v(476.5, -114.3) * mm});
            skPoint(sketch, "E288.middle", {"position": v(482.6, -117.48) * mm});
            skLineSegment(sketch, "E289.bottom", {"start": v(336.3, -190.5) * mm, "end": v(324.1, -190.5) * mm});
            skLineSegment(sketch, "E289.top", {"start": v(336.3, -184.15) * mm, "end": v(324.1, -184.15) * mm});
            skLineSegment(sketch, "E289.left", {"start": v(336.3, -190.5) * mm, "end": v(336.3, -184.15) * mm});
            skLineSegment(sketch, "E289.right", {"start": v(324.1, -190.5) * mm, "end": v(324.1, -184.15) * mm});
            skPoint(sketch, "E289.middle", {"position": v(330.2, -187.33) * mm});
            skLineSegment(sketch, "E290.bottom", {"start": v(183.9, -190.5) * mm, "end": v(171.7, -190.5) * mm});
            skLineSegment(sketch, "E290.top", {"start": v(183.9, -184.15) * mm, "end": v(171.7, -184.15) * mm});
            skLineSegment(sketch, "E290.left", {"start": v(183.9, -190.5) * mm, "end": v(183.9, -184.15) * mm});
            skLineSegment(sketch, "E290.right", {"start": v(171.7, -190.5) * mm, "end": v(171.7, -184.15) * mm});
            skPoint(sketch, "E290.middle", {"position": v(177.8, -187.33) * mm});
            skLineSegment(sketch, "E291.bottom", {"start": v(488.7, -190.5) * mm, "end": v(476.5, -190.5) * mm});
            skLineSegment(sketch, "E291.top", {"start": v(488.7, -184.15) * mm, "end": v(476.5, -184.15) * mm});
            skLineSegment(sketch, "E291.left", {"start": v(488.7, -190.5) * mm, "end": v(488.7, -184.15) * mm});
            skLineSegment(sketch, "E291.right", {"start": v(476.5, -190.5) * mm, "end": v(476.5, -184.15) * mm});
            skPoint(sketch, "E291.middle", {"position": v(482.6, -187.33) * mm});
            skSolve(sketch);
        }
        {
            var Q0;
            Q0 = qSketchRegion(id + "F0", true);
            extrude(context, id + "F1", {"entities" : qUnion([Q0]), "depth" : 3.17 * mm, "offsetDistance" : 25.4 * mm});
        }
        {
            var Q0;
            Q0=qCreatedBy(makeId("Top.planeOp"),FACE);
            var sketch = newSketch(context, id + "F2", { "sketchPlane" : qUnion([Q0])});
            skLineSegment(sketch, "E292", {"start": v(3.18, 75.7) * mm, "end": v(3.18, 82.04) * mm});
            skLineSegment(sketch, "E293", {"start": v(3.18, 82.04) * mm, "end": v(0, 82.04) * mm});
            skLineSegment(sketch, "E294", {"start": v(0, 82.04) * mm, "end": v(0, 101.1) * mm});
            skLineSegment(sketch, "E295", {"start": v(0, 101.1) * mm, "end": v(3.17, 101.1) * mm});
            skLineSegment(sketch, "E296", {"start": v(3.17, 101.1) * mm, "end": v(3.17, 107.44) * mm});
            skLineSegment(sketch, "E297", {"start": v(657.23, 107.44) * mm, "end": v(657.23, 101.1) * mm});
            skLineSegment(sketch, "E298", {"start": v(657.23, 101.1) * mm, "end": v(660.4, 101.1) * mm});
            skLineSegment(sketch, "E299", {"start": v(660.4, 101.1) * mm, "end": v(660.4, 82.04) * mm});
            skLineSegment(sketch, "E300", {"start": v(660.4, 82.04) * mm, "end": v(657.23, 82.04) * mm});
            skLineSegment(sketch, "E301", {"start": v(657.23, 82.04) * mm, "end": v(657.23, 75.7) * mm});
            skLineSegment(sketch, "E302", {"start": v(3.17, 107.44) * mm, "end": v(171.45, 107.44) * mm});
            skLineSegment(sketch, "E303", {"start": v(171.45, 107.44) * mm, "end": v(171.45, 110.62) * mm});
            skLineSegment(sketch, "E304", {"start": v(171.45, 110.62) * mm, "end": v(184.15, 110.62) * mm});
            skLineSegment(sketch, "E305", {"start": v(184.15, 110.62) * mm, "end": v(184.15, 107.44) * mm});
            skLineSegment(sketch, "E306", {"start": v(184.15, 107.44) * mm, "end": v(323.85, 107.44) * mm});
            skLineSegment(sketch, "E307", {"start": v(323.85, 107.44) * mm, "end": v(323.85, 110.62) * mm});
            skLineSegment(sketch, "E308", {"start": v(323.85, 110.62) * mm, "end": v(336.55, 110.62) * mm});
            skLineSegment(sketch, "E309", {"start": v(336.55, 110.62) * mm, "end": v(336.55, 107.44) * mm});
            skLineSegment(sketch, "E310", {"start": v(336.55, 107.44) * mm, "end": v(476.25, 107.44) * mm});
            skLineSegment(sketch, "E311", {"start": v(476.25, 107.44) * mm, "end": v(476.25, 110.62) * mm});
            skLineSegment(sketch, "E312", {"start": v(476.25, 110.62) * mm, "end": v(488.95, 110.62) * mm});
            skLineSegment(sketch, "E313", {"start": v(488.95, 110.62) * mm, "end": v(488.95, 107.44) * mm});
            skLineSegment(sketch, "E314", {"start": v(488.95, 107.44) * mm, "end": v(657.23, 107.44) * mm});
            skLineSegment(sketch, "E315", {"start": v(488.95, 75.7) * mm, "end": v(488.95, 72.52) * mm});
            skLineSegment(sketch, "E316", {"start": v(488.95, 72.52) * mm, "end": v(476.25, 72.52) * mm});
            skLineSegment(sketch, "E317", {"start": v(476.25, 72.52) * mm, "end": v(476.25, 75.7) * mm});
            skLineSegment(sketch, "E318", {"start": v(336.55, 75.7) * mm, "end": v(336.55, 72.52) * mm});
            skLineSegment(sketch, "E319", {"start": v(336.55, 72.52) * mm, "end": v(323.85, 72.52) * mm});
            skLineSegment(sketch, "E320", {"start": v(323.85, 72.52) * mm, "end": v(323.85, 75.7) * mm});
            skLineSegment(sketch, "E321", {"start": v(184.15, 75.7) * mm, "end": v(184.15, 72.52) * mm});
            skLineSegment(sketch, "E322", {"start": v(184.15, 72.52) * mm, "end": v(171.45, 72.52) * mm});
            skLineSegment(sketch, "E323", {"start": v(171.45, 72.52) * mm, "end": v(171.45, 75.7) * mm});
            skLineSegment(sketch, "E324", {"start": v(476.25, 75.7) * mm, "end": v(384.18, 75.7) * mm});
            skLineSegment(sketch, "E325", {"start": v(384.18, 75.7) * mm, "end": v(384.18, 91.57) * mm});
            skLineSegment(sketch, "E326", {"start": v(384.18, 91.57) * mm, "end": v(377.83, 91.57) * mm});
            skLineSegment(sketch, "E327", {"start": v(377.83, 91.57) * mm, "end": v(377.83, 75.7) * mm});
            skLineSegment(sketch, "E328", {"start": v(377.83, 75.7) * mm, "end": v(336.55, 75.7) * mm});
            skLineSegment(sketch, "E329", {"start": v(323.85, 75.7) * mm, "end": v(282.58, 75.7) * mm});
            skLineSegment(sketch, "E330", {"start": v(282.58, 75.7) * mm, "end": v(282.58, 91.57) * mm});
            skLineSegment(sketch, "E331", {"start": v(282.58, 91.57) * mm, "end": v(276.23, 91.57) * mm});
            skLineSegment(sketch, "E332", {"start": v(276.23, 91.57) * mm, "end": v(276.23, 75.7) * mm});
            skLineSegment(sketch, "E333", {"start": v(276.23, 75.7) * mm, "end": v(184.15, 75.7) * mm});
            skLineSegment(sketch, "E334", {"start": v(3.18, 75.7) * mm, "end": v(123.82, 75.7) * mm});
            skLineSegment(sketch, "E335", {"start": v(123.82, 75.7) * mm, "end": v(123.82, 91.57) * mm});
            skLineSegment(sketch, "E336", {"start": v(123.83, 91.57) * mm, "end": v(130.18, 91.57) * mm});
            skLineSegment(sketch, "E337", {"start": v(130.18, 91.57) * mm, "end": v(130.18, 75.7) * mm});
            skLineSegment(sketch, "E338", {"start": v(130.18, 75.7) * mm, "end": v(171.45, 75.7) * mm});
            skLineSegment(sketch, "E339", {"start": v(657.23, 75.7) * mm, "end": v(536.58, 75.7) * mm});
            skLineSegment(sketch, "E340", {"start": v(536.58, 75.7) * mm, "end": v(536.58, 91.57) * mm});
            skLineSegment(sketch, "E341", {"start": v(536.58, 91.57) * mm, "end": v(530.23, 91.57) * mm});
            skLineSegment(sketch, "E342", {"start": v(530.23, 91.57) * mm, "end": v(530.23, 75.7) * mm});
            skLineSegment(sketch, "E343", {"start": v(488.95, 75.7) * mm, "end": v(530.23, 75.7) * mm});
            skSolve(sketch);
        }
        {
            var Q0;
            Q0=makeQuery(id+"F2.imprint","IMPRINT",FACE,{"disambiguationData":[TD([[makeQuery(id+"F2.imprint","IMPRINT",EDGE,{"derivedFrom":sQuery(id+"F2.wireOp",EDGE,"E292")}),-1.0]])]});
            extrude(context, id + "F3", {"entities" : qUnion([Q0]), "depth" : 6.35 * mm, "offsetDistance" : 25.4 * mm});
        }
        {
            var Q0;
            Q0=qCreatedBy(makeId("Top.planeOp"),FACE);
            var sketch = newSketch(context, id + "F4", { "sketchPlane" : qUnion([Q0])});
            skLineSegment(sketch, "E344", {"start": v(96.41, 242.84) * mm, "end": v(96.41, 246.01) * mm});
            skLineSegment(sketch, "E345", {"start": v(96.41, 246.01) * mm, "end": v(109.11, 246.01) * mm});
            skLineSegment(sketch, "E346", {"start": v(109.11, 246.01) * mm, "end": v(109.11, 242.84) * mm});
            skLineSegment(sketch, "E347", {"start": v(109.11, 242.84) * mm, "end": v(248.81, 242.84) * mm});
            skLineSegment(sketch, "E348", {"start": v(248.81, 242.84) * mm, "end": v(248.81, 246.01) * mm});
            skLineSegment(sketch, "E349", {"start": v(248.81, 246.01) * mm, "end": v(261.51, 246.01) * mm});
            skLineSegment(sketch, "E350", {"start": v(261.51, 246.01) * mm, "end": v(261.51, 242.84) * mm});
            skLineSegment(sketch, "E351", {"start": v(261.51, 242.84) * mm, "end": v(401.21, 242.84) * mm});
            skLineSegment(sketch, "E352", {"start": v(401.21, 242.84) * mm, "end": v(401.21, 246.01) * mm});
            skLineSegment(sketch, "E353", {"start": v(401.21, 246.01) * mm, "end": v(413.91, 246.01) * mm});
            skLineSegment(sketch, "E354", {"start": v(413.91, 246.01) * mm, "end": v(413.91, 242.84) * mm});
            skLineSegment(sketch, "E355", {"start": v(413.91, 211.09) * mm, "end": v(413.91, 207.91) * mm});
            skLineSegment(sketch, "E356", {"start": v(413.91, 207.91) * mm, "end": v(401.21, 207.91) * mm});
            skLineSegment(sketch, "E357", {"start": v(401.21, 207.91) * mm, "end": v(401.21, 211.09) * mm});
            skLineSegment(sketch, "E358", {"start": v(261.51, 211.09) * mm, "end": v(261.51, 207.91) * mm});
            skLineSegment(sketch, "E359", {"start": v(261.51, 207.91) * mm, "end": v(248.81, 207.91) * mm});
            skLineSegment(sketch, "E360", {"start": v(248.81, 207.91) * mm, "end": v(248.81, 211.09) * mm});
            skLineSegment(sketch, "E361", {"start": v(109.11, 211.09) * mm, "end": v(109.11, 207.91) * mm});
            skLineSegment(sketch, "E362", {"start": v(109.11, 207.91) * mm, "end": v(96.41, 207.91) * mm});
            skLineSegment(sketch, "E363", {"start": v(96.41, 207.91) * mm, "end": v(96.41, 211.09) * mm});
            skLineSegment(sketch, "E364", {"start": v(401.21, 211.09) * mm, "end": v(309.14, 211.09) * mm});
            skLineSegment(sketch, "E365", {"start": v(309.14, 211.09) * mm, "end": v(309.14, 226.96) * mm});
            skLineSegment(sketch, "E366", {"start": v(309.14, 226.96) * mm, "end": v(302.79, 226.96) * mm});
            skLineSegment(sketch, "E367", {"start": v(302.79, 226.96) * mm, "end": v(302.79, 211.09) * mm});
            skLineSegment(sketch, "E368", {"start": v(302.79, 211.09) * mm, "end": v(261.51, 211.09) * mm});
            skLineSegment(sketch, "E369", {"start": v(248.81, 211.09) * mm, "end": v(207.54, 211.09) * mm});
            skLineSegment(sketch, "E370", {"start": v(207.54, 211.09) * mm, "end": v(207.54, 226.96) * mm});
            skLineSegment(sketch, "E371", {"start": v(207.54, 226.96) * mm, "end": v(201.19, 226.96) * mm});
            skLineSegment(sketch, "E372", {"start": v(201.19, 226.96) * mm, "end": v(201.19, 211.09) * mm});
            skLineSegment(sketch, "E373", {"start": v(201.19, 211.09) * mm, "end": v(109.11, 211.09) * mm});
            skLineSegment(sketch, "E374", {"start": v(48.79, 211.09) * mm, "end": v(48.79, 226.96) * mm});
            skLineSegment(sketch, "E375", {"start": v(48.79, 226.96) * mm, "end": v(55.14, 226.96) * mm});
            skLineSegment(sketch, "E376", {"start": v(55.14, 226.96) * mm, "end": v(55.14, 211.09) * mm});
            skLineSegment(sketch, "E377", {"start": v(55.14, 211.09) * mm, "end": v(96.41, 211.09) * mm});
            skLineSegment(sketch, "E378", {"start": v(461.54, 211.09) * mm, "end": v(461.54, 226.96) * mm});
            skLineSegment(sketch, "E379", {"start": v(461.54, 226.96) * mm, "end": v(455.19, 226.96) * mm});
            skLineSegment(sketch, "E380", {"start": v(455.19, 226.96) * mm, "end": v(455.19, 211.09) * mm});
            skLineSegment(sketch, "E381", {"start": v(413.91, 211.09) * mm, "end": v(455.19, 211.09) * mm});
            skLineSegment(sketch, "E382", {"start": v(-21.06, 211.09) * mm, "end": v(-21.06, 217.44) * mm});
            skLineSegment(sketch, "E383", {"start": v(-21.06, 217.44) * mm, "end": v(-24.24, 217.44) * mm});
            skLineSegment(sketch, "E384", {"start": v(-24.24, 217.44) * mm, "end": v(-24.24, 236.49) * mm});
            skLineSegment(sketch, "E385", {"start": v(-24.24, 236.49) * mm, "end": v(-21.06, 236.49) * mm});
            skLineSegment(sketch, "E386", {"start": v(-21.06, 236.49) * mm, "end": v(-21.06, 242.84) * mm});
            skLineSegment(sketch, "E387", {"start": v(-21.06, 242.84) * mm, "end": v(96.41, 242.84) * mm});
            skLineSegment(sketch, "E388", {"start": v(48.79, 211.09) * mm, "end": v(-21.06, 211.09) * mm});
            skLineSegment(sketch, "E389", {"start": v(531.39, 242.84) * mm, "end": v(531.39, 236.49) * mm});
            skLineSegment(sketch, "E390", {"start": v(531.39, 236.49) * mm, "end": v(534.56, 236.49) * mm});
            skLineSegment(sketch, "E391", {"start": v(534.56, 236.49) * mm, "end": v(534.56, 217.44) * mm});
            skLineSegment(sketch, "E392", {"start": v(534.56, 217.44) * mm, "end": v(531.39, 217.44) * mm});
            skLineSegment(sketch, "E393", {"start": v(531.39, 217.44) * mm, "end": v(531.39, 211.09) * mm});
            skLineSegment(sketch, "E394", {"start": v(413.91, 242.84) * mm, "end": v(531.39, 242.84) * mm});
            skLineSegment(sketch, "E395", {"start": v(531.39, 211.09) * mm, "end": v(461.54, 211.09) * mm});
            skSolve(sketch);
        }
        {
            var Q0;
            Q0 = qSketchRegion(id + "F4", true);
            extrude(context, id + "F5", {"entities" : qUnion([Q0]), "depth" : 6.35 * mm, "offsetDistance" : 25.4 * mm});
        }
        {
            var Q0;
            Q0=qCreatedBy(makeId("Top.planeOp"),FACE);
            var sketch = newSketch(context, id + "F6", { "sketchPlane" : qUnion([Q0])});
            skLineSegment(sketch, "E396", {"start": v(761.76, 246.02) * mm, "end": v(761.76, 249.2) * mm});
            skLineSegment(sketch, "E397", {"start": v(761.76, 249.2) * mm, "end": v(774.46, 249.2) * mm});
            skLineSegment(sketch, "E398", {"start": v(774.46, 249.2) * mm, "end": v(774.46, 246.02) * mm});
            skLineSegment(sketch, "E399.bottom", {"start": v(964.96, 249.2) * mm, "end": v(977.66, 249.2) * mm});
            skLineSegment(sketch, "E399.left", {"start": v(964.96, 249.2) * mm, "end": v(964.96, 246.02) * mm});
            skLineSegment(sketch, "E399.right", {"start": v(977.66, 249.2) * mm, "end": v(977.66, 246.02) * mm});
            skLineSegment(sketch, "E400", {"start": v(977.66, 214.27) * mm, "end": v(977.66, 211.1) * mm});
            skLineSegment(sketch, "E401", {"start": v(977.66, 211.1) * mm, "end": v(964.96, 211.1) * mm});
            skLineSegment(sketch, "E402", {"start": v(964.96, 211.1) * mm, "end": v(964.96, 214.27) * mm});
            skLineSegment(sketch, "E403.bottom", {"start": v(774.46, 211.1) * mm, "end": v(761.76, 211.1) * mm});
            skLineSegment(sketch, "E403.left", {"start": v(774.46, 211.1) * mm, "end": v(774.46, 214.27) * mm});
            skLineSegment(sketch, "E403.right", {"start": v(761.76, 211.1) * mm, "end": v(761.76, 214.27) * mm});
            skLineSegment(sketch, "E404", {"start": v(739.53, 246.02) * mm, "end": v(739.53, 230.15) * mm});
            skLineSegment(sketch, "E405", {"start": v(739.53, 230.15) * mm, "end": v(745.88, 230.15) * mm});
            skLineSegment(sketch, "E406", {"start": v(745.88, 230.15) * mm, "end": v(745.88, 246.02) * mm});
            skLineSegment(sketch, "E407", {"start": v(745.88, 246.02) * mm, "end": v(761.76, 246.02) * mm});
            skLineSegment(sketch, "E408", {"start": v(774.46, 246.02) * mm, "end": v(790.33, 246.02) * mm});
            skLineSegment(sketch, "E409", {"start": v(790.33, 246.02) * mm, "end": v(790.33, 230.15) * mm});
            skLineSegment(sketch, "E410", {"start": v(790.33, 230.15) * mm, "end": v(796.68, 230.15) * mm});
            skLineSegment(sketch, "E411", {"start": v(796.68, 230.15) * mm, "end": v(796.68, 246.02) * mm});
            skLineSegment(sketch, "E412", {"start": v(796.68, 246.02) * mm, "end": v(831.6, 246.02) * mm});
            skLineSegment(sketch, "E413", {"start": v(831.6, 246.02) * mm, "end": v(831.6, 230.15) * mm});
            skLineSegment(sketch, "E414", {"start": v(831.6, 230.15) * mm, "end": v(837.96, 230.15) * mm});
            skLineSegment(sketch, "E415", {"start": v(837.96, 230.15) * mm, "end": v(837.96, 246.02) * mm});
            skLineSegment(sketch, "E416", {"start": v(837.96, 246.02) * mm, "end": v(866.53, 246.02) * mm});
            skLineSegment(sketch, "E417", {"start": v(866.53, 246.02) * mm, "end": v(866.53, 230.15) * mm});
            skLineSegment(sketch, "E418", {"start": v(866.53, 230.15) * mm, "end": v(872.88, 230.15) * mm});
            skLineSegment(sketch, "E419", {"start": v(872.88, 230.15) * mm, "end": v(872.88, 246.02) * mm});
            skLineSegment(sketch, "E420", {"start": v(872.88, 246.02) * mm, "end": v(901.46, 246.02) * mm});
            skLineSegment(sketch, "E421", {"start": v(901.46, 246.02) * mm, "end": v(901.46, 230.15) * mm});
            skLineSegment(sketch, "E422", {"start": v(901.46, 230.15) * mm, "end": v(907.8, 230.15) * mm});
            skLineSegment(sketch, "E423", {"start": v(907.8, 230.15) * mm, "end": v(907.8, 246.02) * mm});
            skLineSegment(sketch, "E424", {"start": v(907.8, 246.02) * mm, "end": v(942.73, 246.02) * mm});
            skLineSegment(sketch, "E425", {"start": v(942.73, 246.02) * mm, "end": v(942.73, 230.15) * mm});
            skLineSegment(sketch, "E426", {"start": v(942.73, 230.15) * mm, "end": v(949.08, 230.15) * mm});
            skLineSegment(sketch, "E427", {"start": v(949.08, 230.15) * mm, "end": v(949.08, 246.02) * mm});
            skLineSegment(sketch, "E428", {"start": v(949.08, 246.02) * mm, "end": v(964.96, 246.02) * mm});
            skLineSegment(sketch, "E429", {"start": v(977.66, 246.02) * mm, "end": v(993.53, 246.02) * mm});
            skLineSegment(sketch, "E430", {"start": v(993.53, 246.02) * mm, "end": v(993.53, 230.15) * mm});
            skLineSegment(sketch, "E431", {"start": v(993.53, 230.15) * mm, "end": v(999.88, 230.15) * mm});
            skLineSegment(sketch, "E432", {"start": v(999.88, 230.15) * mm, "end": v(999.88, 246.02) * mm});
            skLineSegment(sketch, "E433", {"start": v(774.46, 214.27) * mm, "end": v(964.96, 214.27) * mm});
            skLineSegment(sketch, "E434.top", {"start": v(717.3, 220.62) * mm, "end": v(720.48, 220.62) * mm});
            skLineSegment(sketch, "E434.right", {"start": v(720.48, 214.27) * mm, "end": v(720.48, 220.62) * mm});
            skLineSegment(sketch, "E435.top", {"start": v(717.3, 239.67) * mm, "end": v(720.48, 239.67) * mm});
            skLineSegment(sketch, "E435.right", {"start": v(720.48, 246.02) * mm, "end": v(720.48, 239.67) * mm});
            skLineSegment(sketch, "E436", {"start": v(717.3, 220.62) * mm, "end": v(717.3, 239.67) * mm});
            skLineSegment(sketch, "E437", {"start": v(720.48, 214.27) * mm, "end": v(761.76, 214.27) * mm});
            skLineSegment(sketch, "E438", {"start": v(720.48, 246.02) * mm, "end": v(739.53, 246.02) * mm});
            skLineSegment(sketch, "E439.top", {"start": v(1022.1, 239.67) * mm, "end": v(1018.93, 239.67) * mm});
            skLineSegment(sketch, "E439.right", {"start": v(1018.93, 246.02) * mm, "end": v(1018.93, 239.67) * mm});
            skLineSegment(sketch, "E440.top", {"start": v(1022.1, 220.62) * mm, "end": v(1018.93, 220.62) * mm});
            skLineSegment(sketch, "E440.right", {"start": v(1018.93, 214.27) * mm, "end": v(1018.93, 220.62) * mm});
            skLineSegment(sketch, "E441", {"start": v(1022.1, 239.67) * mm, "end": v(1022.1, 220.62) * mm});
            skLineSegment(sketch, "E442", {"start": v(999.88, 246.02) * mm, "end": v(1018.93, 246.02) * mm});
            skLineSegment(sketch, "E443", {"start": v(1018.93, 214.27) * mm, "end": v(977.66, 214.27) * mm});
            skSolve(sketch);
        }
        {
            var Q0;
            Q0 = qSketchRegion(id + "F6", true);
            extrude(context, id + "F7", {"entities" : qUnion([Q0]), "depth" : 6.35 * mm, "offsetDistance" : 25.4 * mm});
        }
        {
            var Q0;
            Q0=qCreatedBy(makeId("Top.planeOp"),FACE);
            var sketch = newSketch(context, id + "F8", { "sketchPlane" : qUnion([Q0])});
            skLineSegment(sketch, "E444.bottom", {"start": v(675.85, -147.16) * mm, "end": v(726.65, -147.16) * mm});
            skLineSegment(sketch, "E444.top", {"start": v(675.85, -197.96) * mm, "end": v(726.65, -197.96) * mm});
            skLineSegment(sketch, "E444.left", {"start": v(675.85, -147.16) * mm, "end": v(675.85, -197.96) * mm});
            skLineSegment(sketch, "E445.bottom", {"start": v(688.55, -153.51) * mm, "end": v(694.9, -153.51) * mm});
            skLineSegment(sketch, "E445.top", {"start": v(688.55, -156.69) * mm, "end": v(694.9, -156.69) * mm});
            skLineSegment(sketch, "E445.left", {"start": v(688.55, -153.51) * mm, "end": v(688.55, -156.69) * mm});
            skLineSegment(sketch, "E445.right", {"start": v(694.9, -153.51) * mm, "end": v(694.9, -156.69) * mm});
            skLineSegment(sketch, "E446.bottom", {"start": v(713.95, -153.51) * mm, "end": v(707.6, -153.51) * mm});
            skLineSegment(sketch, "E446.top", {"start": v(713.95, -156.69) * mm, "end": v(707.6, -156.69) * mm});
            skLineSegment(sketch, "E446.left", {"start": v(713.95, -153.51) * mm, "end": v(713.95, -156.69) * mm});
            skLineSegment(sketch, "E446.right", {"start": v(707.6, -153.51) * mm, "end": v(707.6, -156.69) * mm});
            skLineSegment(sketch, "E447.bottom", {"start": v(688.55, -188.44) * mm, "end": v(694.9, -188.44) * mm});
            skLineSegment(sketch, "E447.top", {"start": v(688.55, -191.61) * mm, "end": v(694.9, -191.61) * mm});
            skLineSegment(sketch, "E447.left", {"start": v(688.55, -188.44) * mm, "end": v(688.55, -191.61) * mm});
            skLineSegment(sketch, "E447.right", {"start": v(694.9, -188.44) * mm, "end": v(694.9, -191.61) * mm});
            skLineSegment(sketch, "E448.bottom", {"start": v(713.95, -188.44) * mm, "end": v(707.6, -188.44) * mm});
            skLineSegment(sketch, "E448.top", {"start": v(713.95, -191.61) * mm, "end": v(707.6, -191.61) * mm});
            skLineSegment(sketch, "E448.left", {"start": v(713.95, -188.44) * mm, "end": v(713.95, -191.61) * mm});
            skLineSegment(sketch, "E448.right", {"start": v(707.6, -188.44) * mm, "end": v(707.6, -191.61) * mm});
            skPoint(sketch, "E449.middle", {"position": v(726.65, -172.56) * mm});
            skLineSegment(sketch, "E450.bottom", {"start": v(694.9, -181.83) * mm, "end": v(688.55, -181.83) * mm});
            skLineSegment(sketch, "E450.top", {"start": v(694.9, -163.29) * mm, "end": v(688.55, -163.29) * mm});
            skLineSegment(sketch, "E450.left", {"start": v(694.9, -181.83) * mm, "end": v(694.9, -163.29) * mm});
            skLineSegment(sketch, "E450.right", {"start": v(688.55, -181.83) * mm, "end": v(688.55, -163.29) * mm});
            skPoint(sketch, "E450.middle", {"position": v(691.72, -172.56) * mm});
            skLineSegment(sketch, "E451.right", {"start": v(723.47, -181.83) * mm, "end": v(723.47, -163.29) * mm});
            skLineSegment(sketch, "E452", {"start": v(723.47, -163.29) * mm, "end": v(726.65, -163.29) * mm});
            skLineSegment(sketch, "E453", {"start": v(726.65, -163.29) * mm, "end": v(726.65, -147.16) * mm});
            skLineSegment(sketch, "E454", {"start": v(723.47, -181.83) * mm, "end": v(726.65, -181.83) * mm});
            skLineSegment(sketch, "E455", {"start": v(726.65, -181.83) * mm, "end": v(726.65, -197.96) * mm});
            skSolve(sketch);
        }
        {
            var Q0;
            Q0 = qSketchRegion(id + "F8", true);
            extrude(context, id + "F9", {"entities" : qUnion([Q0]), "depth" : 3.17 * mm, "offsetDistance" : 25.4 * mm});
        }
        {
            var Q0;
            Q0=qCreatedBy(makeId("Front.planeOp"),FACE);
            var sketch = newSketch(context, id + "F10", { "sketchPlane" : qUnion([Q0])});
            skLineSegment(sketch, "E456", {"start": v(-451.22, -42.87) * mm, "end": v(-473.45, -42.87) * mm});
            skLineSegment(sketch, "E457", {"start": v(-473.45, -42.87) * mm, "end": v(-473.45, -39.7) * mm});
            skLineSegment(sketch, "E458", {"start": v(-473.45, -39.7) * mm, "end": v(-479.8, -39.7) * mm});
            skLineSegment(sketch, "E459", {"start": v(-479.8, -39.7) * mm, "end": v(-479.8, -42.87) * mm});
            skLineSegment(sketch, "E460", {"start": v(-479.8, -42.87) * mm, "end": v(-502.02, -42.87) * mm});
            skLineSegment(sketch, "E461", {"start": v(-400.42, -42.87) * mm, "end": v(-422.65, -42.87) * mm});
            skLineSegment(sketch, "E462", {"start": v(-422.65, -42.87) * mm, "end": v(-422.65, -39.7) * mm});
            skLineSegment(sketch, "E463", {"start": v(-422.65, -39.7) * mm, "end": v(-429, -39.7) * mm});
            skLineSegment(sketch, "E464", {"start": v(-429, -39.7) * mm, "end": v(-429, -42.87) * mm});
            skLineSegment(sketch, "E465", {"start": v(-429, -42.87) * mm, "end": v(-451.22, -42.87) * mm});
            skLineSegment(sketch, "E466", {"start": v(-349.62, -42.87) * mm, "end": v(-371.85, -42.87) * mm});
            skLineSegment(sketch, "E467", {"start": v(-371.85, -42.87) * mm, "end": v(-371.85, -39.7) * mm});
            skLineSegment(sketch, "E468", {"start": v(-371.85, -39.7) * mm, "end": v(-378.2, -39.7) * mm});
            skLineSegment(sketch, "E469", {"start": v(-378.2, -39.7) * mm, "end": v(-378.2, -42.87) * mm});
            skLineSegment(sketch, "E470", {"start": v(-378.2, -42.87) * mm, "end": v(-400.42, -42.87) * mm});
            skLineSegment(sketch, "E471", {"start": v(56.78, -42.87) * mm, "end": v(34.55, -42.87) * mm});
            skLineSegment(sketch, "E472", {"start": v(34.55, -42.87) * mm, "end": v(34.55, -39.7) * mm});
            skLineSegment(sketch, "E473", {"start": v(34.55, -39.7) * mm, "end": v(28.2, -39.7) * mm});
            skLineSegment(sketch, "E474", {"start": v(28.2, -39.7) * mm, "end": v(28.2, -42.87) * mm});
            skLineSegment(sketch, "E475", {"start": v(28.2, -42.87) * mm, "end": v(5.98, -42.87) * mm});
            skLineSegment(sketch, "E476", {"start": v(107.58, -42.87) * mm, "end": v(85.35, -42.87) * mm});
            skLineSegment(sketch, "E477", {"start": v(85.35, -42.87) * mm, "end": v(85.35, -39.7) * mm});
            skLineSegment(sketch, "E478", {"start": v(85.35, -39.7) * mm, "end": v(79, -39.7) * mm});
            skLineSegment(sketch, "E479", {"start": v(79, -39.7) * mm, "end": v(79, -42.87) * mm});
            skLineSegment(sketch, "E480", {"start": v(79, -42.87) * mm, "end": v(56.78, -42.87) * mm});
            skLineSegment(sketch, "E481", {"start": v(158.38, -42.87) * mm, "end": v(136.15, -42.87) * mm});
            skLineSegment(sketch, "E482", {"start": v(136.15, -42.87) * mm, "end": v(136.15, -39.7) * mm});
            skLineSegment(sketch, "E483", {"start": v(136.15, -39.7) * mm, "end": v(129.8, -39.7) * mm});
            skLineSegment(sketch, "E484", {"start": v(129.8, -39.7) * mm, "end": v(129.8, -42.87) * mm});
            skLineSegment(sketch, "E485", {"start": v(129.8, -42.87) * mm, "end": v(107.58, -42.87) * mm});
            skLineSegment(sketch, "E486", {"start": v(-95.62, -42.87) * mm, "end": v(-117.85, -42.87) * mm});
            skLineSegment(sketch, "E487", {"start": v(-117.85, -42.87) * mm, "end": v(-117.85, -39.7) * mm});
            skLineSegment(sketch, "E488", {"start": v(-117.85, -39.7) * mm, "end": v(-124.2, -39.7) * mm});
            skLineSegment(sketch, "E489", {"start": v(-124.2, -39.7) * mm, "end": v(-124.2, -42.87) * mm});
            skLineSegment(sketch, "E490", {"start": v(-124.2, -42.87) * mm, "end": v(-146.42, -42.87) * mm});
            skLineSegment(sketch, "E491", {"start": v(-44.82, -42.87) * mm, "end": v(-67.05, -42.87) * mm});
            skLineSegment(sketch, "E492", {"start": v(-67.05, -42.87) * mm, "end": v(-67.05, -39.7) * mm});
            skLineSegment(sketch, "E493", {"start": v(-67.05, -39.7) * mm, "end": v(-73.4, -39.7) * mm});
            skLineSegment(sketch, "E494", {"start": v(-73.4, -39.7) * mm, "end": v(-73.4, -42.87) * mm});
            skLineSegment(sketch, "E495", {"start": v(-73.4, -42.87) * mm, "end": v(-95.62, -42.87) * mm});
            skLineSegment(sketch, "E496", {"start": v(5.98, -42.87) * mm, "end": v(-16.25, -42.87) * mm});
            skLineSegment(sketch, "E497", {"start": v(-16.25, -42.87) * mm, "end": v(-16.25, -39.7) * mm});
            skLineSegment(sketch, "E498", {"start": v(-16.25, -39.7) * mm, "end": v(-22.6, -39.7) * mm});
            skLineSegment(sketch, "E499", {"start": v(-22.6, -39.7) * mm, "end": v(-22.6, -42.87) * mm});
            skLineSegment(sketch, "E500", {"start": v(-22.6, -42.87) * mm, "end": v(-44.82, -42.87) * mm});
            skLineSegment(sketch, "E501", {"start": v(-248.02, -42.87) * mm, "end": v(-270.25, -42.87) * mm});
            skLineSegment(sketch, "E502", {"start": v(-270.25, -42.87) * mm, "end": v(-270.25, -39.7) * mm});
            skLineSegment(sketch, "E503", {"start": v(-270.25, -39.7) * mm, "end": v(-276.6, -39.7) * mm});
            skLineSegment(sketch, "E504", {"start": v(-276.6, -39.7) * mm, "end": v(-276.6, -42.87) * mm});
            skLineSegment(sketch, "E505", {"start": v(-276.6, -42.87) * mm, "end": v(-298.82, -42.87) * mm});
            skLineSegment(sketch, "E506", {"start": v(-197.22, -42.87) * mm, "end": v(-219.45, -42.87) * mm});
            skLineSegment(sketch, "E507", {"start": v(-219.45, -42.87) * mm, "end": v(-219.45, -39.7) * mm});
            skLineSegment(sketch, "E508", {"start": v(-219.45, -39.7) * mm, "end": v(-225.8, -39.7) * mm});
            skLineSegment(sketch, "E509", {"start": v(-225.8, -39.7) * mm, "end": v(-225.8, -42.87) * mm});
            skLineSegment(sketch, "E510", {"start": v(-225.8, -42.87) * mm, "end": v(-248.02, -42.87) * mm});
            skLineSegment(sketch, "E511", {"start": v(-146.42, -42.87) * mm, "end": v(-168.65, -42.87) * mm});
            skLineSegment(sketch, "E512", {"start": v(-168.65, -42.87) * mm, "end": v(-168.65, -39.7) * mm});
            skLineSegment(sketch, "E513", {"start": v(-168.65, -39.7) * mm, "end": v(-175, -39.7) * mm});
            skLineSegment(sketch, "E514", {"start": v(-175, -39.7) * mm, "end": v(-175, -42.87) * mm});
            skLineSegment(sketch, "E515", {"start": v(-175, -42.87) * mm, "end": v(-197.22, -42.87) * mm});
            skLineSegment(sketch, "E516", {"start": v(-298.82, -42.87) * mm, "end": v(-321.05, -42.87) * mm});
            skLineSegment(sketch, "E517", {"start": v(-321.05, -42.87) * mm, "end": v(-321.05, -39.7) * mm});
            skLineSegment(sketch, "E518", {"start": v(-321.05, -39.7) * mm, "end": v(-327.4, -39.7) * mm});
            skLineSegment(sketch, "E519", {"start": v(-327.4, -39.7) * mm, "end": v(-327.4, -42.87) * mm});
            skLineSegment(sketch, "E520", {"start": v(-327.4, -42.87) * mm, "end": v(-349.62, -42.87) * mm});
            skPoint(sketch, "E521", {"position": v(31.38, -39.7) * mm});
            skLineSegment(sketch, "E522", {"start": v(107.58, -74.62) * mm, "end": v(129.8, -74.62) * mm});
            skLineSegment(sketch, "E523", {"start": v(129.8, -74.62) * mm, "end": v(129.8, -77.8) * mm});
            skLineSegment(sketch, "E524", {"start": v(129.8, -77.8) * mm, "end": v(136.15, -77.8) * mm});
            skLineSegment(sketch, "E525", {"start": v(136.15, -77.8) * mm, "end": v(136.15, -74.62) * mm});
            skLineSegment(sketch, "E526", {"start": v(136.15, -74.62) * mm, "end": v(158.38, -74.62) * mm});
            skLineSegment(sketch, "E527", {"start": v(56.78, -74.62) * mm, "end": v(79, -74.62) * mm});
            skLineSegment(sketch, "E528", {"start": v(79, -74.62) * mm, "end": v(79, -77.8) * mm});
            skLineSegment(sketch, "E529", {"start": v(79, -77.8) * mm, "end": v(85.35, -77.8) * mm});
            skLineSegment(sketch, "E530", {"start": v(85.35, -77.8) * mm, "end": v(85.35, -74.62) * mm});
            skLineSegment(sketch, "E531", {"start": v(85.35, -74.62) * mm, "end": v(107.58, -74.62) * mm});
            skLineSegment(sketch, "E532", {"start": v(5.98, -74.62) * mm, "end": v(28.2, -74.62) * mm});
            skLineSegment(sketch, "E533", {"start": v(28.2, -74.62) * mm, "end": v(28.2, -77.8) * mm});
            skLineSegment(sketch, "E534", {"start": v(28.2, -77.8) * mm, "end": v(34.55, -77.8) * mm});
            skLineSegment(sketch, "E535", {"start": v(34.55, -77.8) * mm, "end": v(34.55, -74.62) * mm});
            skLineSegment(sketch, "E536", {"start": v(34.55, -74.62) * mm, "end": v(56.78, -74.62) * mm});
            skLineSegment(sketch, "E537", {"start": v(-400.42, -74.62) * mm, "end": v(-378.2, -74.62) * mm});
            skLineSegment(sketch, "E538", {"start": v(-378.2, -74.62) * mm, "end": v(-378.2, -77.8) * mm});
            skLineSegment(sketch, "E539", {"start": v(-378.2, -77.8) * mm, "end": v(-371.85, -77.8) * mm});
            skLineSegment(sketch, "E540", {"start": v(-371.85, -77.8) * mm, "end": v(-371.85, -74.62) * mm});
            skLineSegment(sketch, "E541", {"start": v(-371.85, -74.62) * mm, "end": v(-349.62, -74.62) * mm});
            skLineSegment(sketch, "E542", {"start": v(-451.22, -74.62) * mm, "end": v(-429, -74.62) * mm});
            skLineSegment(sketch, "E543", {"start": v(-429, -74.62) * mm, "end": v(-429, -77.8) * mm});
            skLineSegment(sketch, "E544", {"start": v(-429, -77.8) * mm, "end": v(-422.65, -77.8) * mm});
            skLineSegment(sketch, "E545", {"start": v(-422.65, -77.8) * mm, "end": v(-422.65, -74.62) * mm});
            skLineSegment(sketch, "E546", {"start": v(-422.65, -74.62) * mm, "end": v(-400.42, -74.62) * mm});
            skLineSegment(sketch, "E547", {"start": v(-502.02, -74.62) * mm, "end": v(-479.8, -74.62) * mm});
            skLineSegment(sketch, "E548", {"start": v(-479.8, -74.62) * mm, "end": v(-479.8, -77.8) * mm});
            skLineSegment(sketch, "E549", {"start": v(-479.8, -77.8) * mm, "end": v(-473.45, -77.8) * mm});
            skLineSegment(sketch, "E550", {"start": v(-473.45, -77.8) * mm, "end": v(-473.45, -74.62) * mm});
            skLineSegment(sketch, "E551", {"start": v(-473.45, -74.62) * mm, "end": v(-451.22, -74.62) * mm});
            skLineSegment(sketch, "E552", {"start": v(-248.02, -74.62) * mm, "end": v(-225.8, -74.62) * mm});
            skLineSegment(sketch, "E553", {"start": v(-225.8, -74.62) * mm, "end": v(-225.8, -77.8) * mm});
            skLineSegment(sketch, "E554", {"start": v(-225.8, -77.8) * mm, "end": v(-219.45, -77.8) * mm});
            skLineSegment(sketch, "E555", {"start": v(-219.45, -77.8) * mm, "end": v(-219.45, -74.62) * mm});
            skLineSegment(sketch, "E556", {"start": v(-219.45, -74.62) * mm, "end": v(-197.22, -74.62) * mm});
            skLineSegment(sketch, "E557", {"start": v(-298.82, -74.62) * mm, "end": v(-276.6, -74.62) * mm});
            skLineSegment(sketch, "E558", {"start": v(-276.6, -74.62) * mm, "end": v(-276.6, -77.8) * mm});
            skLineSegment(sketch, "E559", {"start": v(-276.6, -77.8) * mm, "end": v(-270.25, -77.8) * mm});
            skLineSegment(sketch, "E560", {"start": v(-270.25, -77.8) * mm, "end": v(-270.25, -74.62) * mm});
            skLineSegment(sketch, "E561", {"start": v(-270.25, -74.62) * mm, "end": v(-248.02, -74.62) * mm});
            skLineSegment(sketch, "E562", {"start": v(-349.62, -74.62) * mm, "end": v(-327.4, -74.62) * mm});
            skLineSegment(sketch, "E563", {"start": v(-327.4, -74.62) * mm, "end": v(-327.4, -77.8) * mm});
            skLineSegment(sketch, "E564", {"start": v(-327.4, -77.8) * mm, "end": v(-321.05, -77.8) * mm});
            skLineSegment(sketch, "E565", {"start": v(-321.05, -77.8) * mm, "end": v(-321.05, -74.62) * mm});
            skLineSegment(sketch, "E566", {"start": v(-321.05, -74.62) * mm, "end": v(-298.82, -74.62) * mm});
            skLineSegment(sketch, "E567", {"start": v(-95.62, -74.62) * mm, "end": v(-73.4, -74.62) * mm});
            skLineSegment(sketch, "E568", {"start": v(-73.4, -74.62) * mm, "end": v(-73.4, -77.8) * mm});
            skLineSegment(sketch, "E569", {"start": v(-73.4, -77.8) * mm, "end": v(-67.05, -77.8) * mm});
            skLineSegment(sketch, "E570", {"start": v(-67.05, -77.8) * mm, "end": v(-67.05, -74.62) * mm});
            skLineSegment(sketch, "E571", {"start": v(-67.05, -74.62) * mm, "end": v(-44.82, -74.62) * mm});
            skLineSegment(sketch, "E572", {"start": v(-146.42, -74.62) * mm, "end": v(-124.2, -74.62) * mm});
            skLineSegment(sketch, "E573", {"start": v(-124.2, -74.62) * mm, "end": v(-124.2, -77.8) * mm});
            skLineSegment(sketch, "E574", {"start": v(-124.2, -77.8) * mm, "end": v(-117.85, -77.8) * mm});
            skLineSegment(sketch, "E575", {"start": v(-117.85, -77.8) * mm, "end": v(-117.85, -74.62) * mm});
            skLineSegment(sketch, "E576", {"start": v(-117.85, -74.62) * mm, "end": v(-95.62, -74.62) * mm});
            skLineSegment(sketch, "E577", {"start": v(-197.22, -74.62) * mm, "end": v(-175, -74.62) * mm});
            skLineSegment(sketch, "E578", {"start": v(-175, -74.62) * mm, "end": v(-175, -77.8) * mm});
            skLineSegment(sketch, "E579", {"start": v(-175, -77.8) * mm, "end": v(-168.65, -77.8) * mm});
            skLineSegment(sketch, "E580", {"start": v(-168.65, -77.8) * mm, "end": v(-168.65, -74.62) * mm});
            skLineSegment(sketch, "E581", {"start": v(-168.65, -74.62) * mm, "end": v(-146.42, -74.62) * mm});
            skLineSegment(sketch, "E582", {"start": v(-44.82, -74.62) * mm, "end": v(-22.6, -74.62) * mm});
            skLineSegment(sketch, "E583", {"start": v(-22.6, -74.62) * mm, "end": v(-22.6, -77.8) * mm});
            skLineSegment(sketch, "E584", {"start": v(-22.6, -77.8) * mm, "end": v(-16.25, -77.8) * mm});
            skLineSegment(sketch, "E585", {"start": v(-16.25, -77.8) * mm, "end": v(-16.25, -74.62) * mm});
            skLineSegment(sketch, "E586", {"start": v(-16.25, -74.62) * mm, "end": v(5.98, -74.62) * mm});
            skPoint(sketch, "E587", {"position": v(-375.02, -77.8) * mm});
            skLineSegment(sketch, "E588", {"start": v(-502.02, -74.62) * mm, "end": v(-502.02, -42.87) * mm});
            skLineSegment(sketch, "E589", {"start": v(158.38, -74.62) * mm, "end": v(158.38, -42.87) * mm});
            skLineSegment(sketch, "E590.bottom", {"start": v(-124.2, -68.02) * mm, "end": v(-117.85, -68.02) * mm});
            skLineSegment(sketch, "E590.top", {"start": v(-124.2, -49.47) * mm, "end": v(-117.85, -49.47) * mm});
            skLineSegment(sketch, "E590.left", {"start": v(-124.2, -68.02) * mm, "end": v(-124.2, -49.47) * mm});
            skLineSegment(sketch, "E590.right", {"start": v(-117.85, -68.02) * mm, "end": v(-117.85, -49.47) * mm});
            skPoint(sketch, "E590.middle", {"position": v(-121.02, -58.75) * mm});
            skPoint(sketch, "E591", {"position": v(-121.02, -77.8) * mm});
            skLineSegment(sketch, "E592.bottom", {"start": v(28.2, -68.02) * mm, "end": v(34.55, -68.02) * mm});
            skLineSegment(sketch, "E592.top", {"start": v(28.2, -49.47) * mm, "end": v(34.55, -49.47) * mm});
            skLineSegment(sketch, "E592.left", {"start": v(28.2, -68.02) * mm, "end": v(28.2, -49.47) * mm});
            skLineSegment(sketch, "E592.right", {"start": v(34.55, -68.02) * mm, "end": v(34.55, -49.47) * mm});
            skPoint(sketch, "E592.middle", {"position": v(31.38, -58.75) * mm});
            skLineSegment(sketch, "E593.bottom", {"start": v(-378.2, -68.02) * mm, "end": v(-371.85, -68.02) * mm});
            skLineSegment(sketch, "E593.top", {"start": v(-378.2, -49.47) * mm, "end": v(-371.85, -49.47) * mm});
            skLineSegment(sketch, "E593.left", {"start": v(-378.2, -68.02) * mm, "end": v(-378.2, -49.47) * mm});
            skLineSegment(sketch, "E593.right", {"start": v(-371.85, -68.02) * mm, "end": v(-371.85, -49.47) * mm});
            skPoint(sketch, "E593.middle", {"position": v(-375.02, -58.75) * mm});
            skLineSegment(sketch, "E594.bottom", {"start": v(-225.8, -68.02) * mm, "end": v(-219.45, -68.02) * mm});
            skLineSegment(sketch, "E594.top", {"start": v(-225.8, -49.47) * mm, "end": v(-219.45, -49.47) * mm});
            skLineSegment(sketch, "E594.left", {"start": v(-225.8, -68.02) * mm, "end": v(-225.8, -49.47) * mm});
            skLineSegment(sketch, "E594.right", {"start": v(-219.45, -68.02) * mm, "end": v(-219.45, -49.47) * mm});
            skPoint(sketch, "E594.middle", {"position": v(-222.62, -58.75) * mm});
            skSolve(sketch);
        }
        {
            var Q0;
            Q0 = qSketchRegion(id + "F10", true);
            extrude(context, id + "F11", {"entities" : qUnion([Q0]), "depth" : 3.17 * mm, "offsetDistance" : 25.4 * mm});
        }
    });
